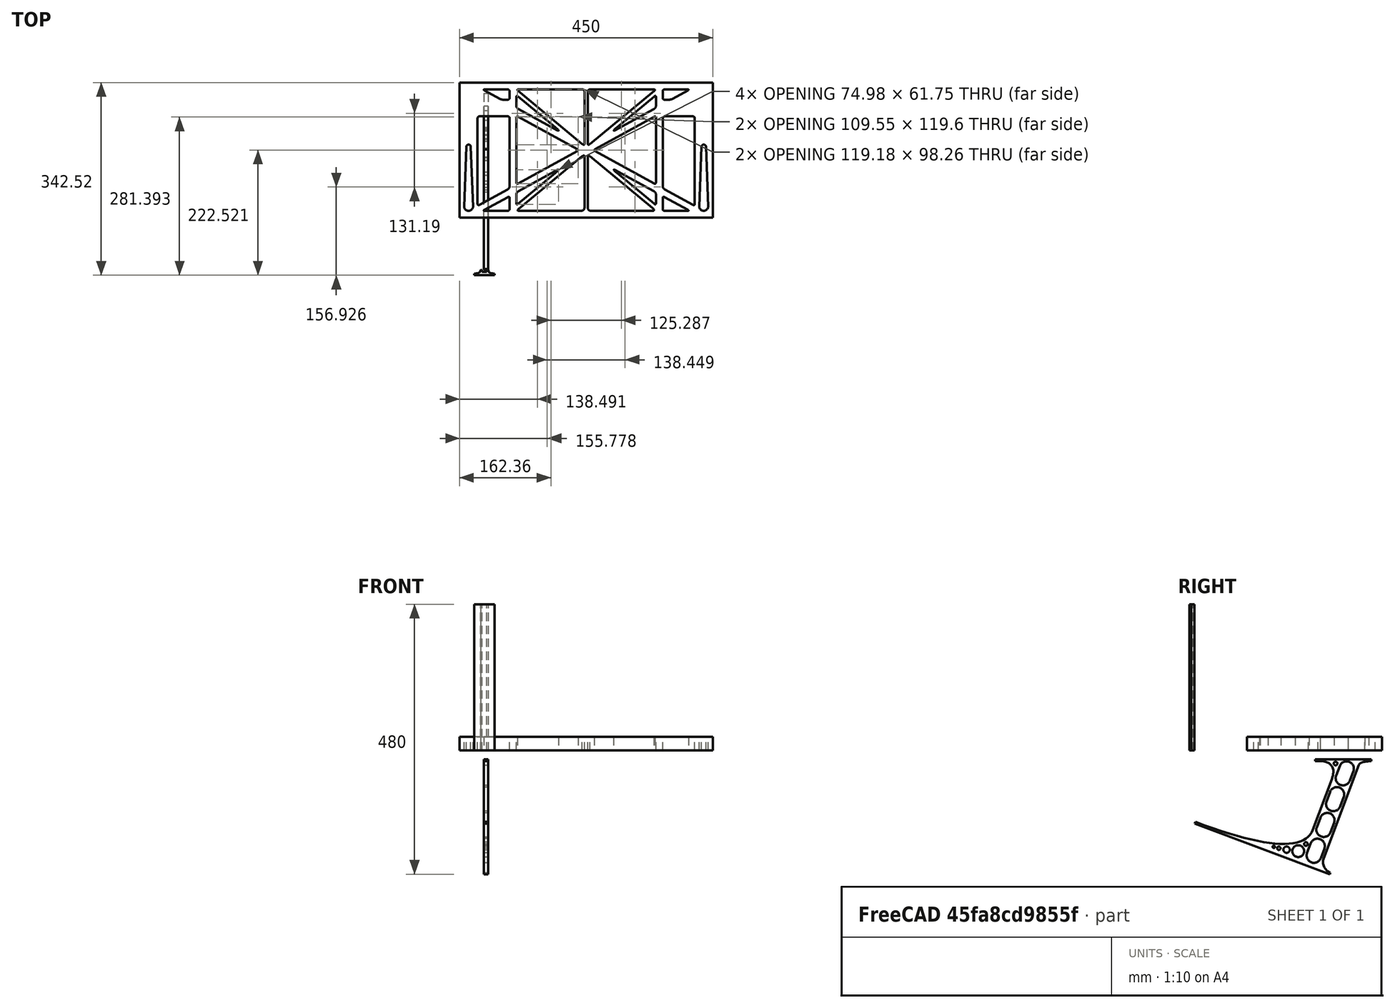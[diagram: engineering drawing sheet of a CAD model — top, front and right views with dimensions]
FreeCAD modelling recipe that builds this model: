
FCSTD DOCUMENT  (FreeCAD 0.19R0.19.2)
Label: laptopStand153FCStd
License: All rights reserved
LicenseURL: http://en.wikipedia.org/wiki/All_rights_reserved
objects: Sketcher::SketchObject×4, Part::Extrusion×3
note: 7 computed .brp shape members not serialized (recipe doc carries the construction recipe); baked Part::Feature solids carry a one-line shape summary decoded from their .brp

FEATURE [Sketcher::SketchObject] Sketch
  FullyConstrained = false
  sketch-geometry (349):
    g0: LineSegment StartX=-10.9272 StartY=-82.7794 StartZ=0 EndX=46.0728 EndY=-51.4823 EndZ=0
    g1: LineSegment StartX=-10.9272 StartY=76.4095 StartZ=0 EndX=-10.9272 EndY=-82.7794 EndZ=0
    g2: LineSegment StartX=46.0728 StartY=76.4095 StartZ=0 EndX=46.0728 EndY=-51.4823 EndZ=0
    g3: LineSegment StartX=-42.9272 StartY=136.221 StartZ=0 EndX=-42.9272 EndY=-103.779 EndZ=0
    g4: LineSegment StartX=407.073 StartY=136.221 StartZ=0 EndX=407.073 EndY=-103.779 EndZ=0
    g5: ArcOfCircle CenterX=-26.9272 CenterY=-83.7794 CenterZ=0 NormalX=0 NormalY=0 NormalZ=1 AngleXU=0 Radius=8 StartAngle=3.14159 EndAngle=6.28319
    g6: ArcOfCircle CenterX=391.073 CenterY=22.1087 CenterZ=0 NormalX=0 NormalY=0 NormalZ=1 AngleXU=0 Radius=8 StartAngle=-4.4e-15 EndAngle=3.14159
    g7: LineSegment StartX=399.073 StartY=22.1087 StartZ=0 EndX=399.073 EndY=-83.7794 EndZ=0
    g8: LineSegment StartX=383.073 StartY=22.1087 StartZ=0 EndX=383.073 EndY=-83.7794 EndZ=0
    g9: ArcOfCircle CenterX=391.073 CenterY=-83.7794 CenterZ=0 NormalX=0 NormalY=0 NormalZ=1 AngleXU=0 Radius=8 StartAngle=3.14159 EndAngle=6.28319
    g10: Circle CenterX=175.022 CenterY=27.0628 CenterZ=0 NormalX=0 NormalY=0 NormalZ=1 AngleXU=0 Radius=1
    g11: Circle CenterX=179.022 CenterY=24.8665 CenterZ=0 NormalX=0 NormalY=0 NormalZ=1 AngleXU=0 Radius=1
    g12: Circle CenterX=179.022 CenterY=27.0628 CenterZ=0 NormalX=0 NormalY=0 NormalZ=1 AngleXU=0 Radius=1
    g13: BSplineCurve PolesCount=3 KnotsCount=2 Degree=2 IsPeriodic=0
    g14: GeomPoint X=175.022 Y=27.0628 Z=0
    g15: GeomPoint X=179.022 Y=27.0628 Z=0
    g16: Circle CenterX=189.124 CenterY=27.0628 CenterZ=0 NormalX=0 NormalY=0 NormalZ=1 AngleXU=0 Radius=1
    g17: Circle CenterX=185.124 CenterY=24.8665 CenterZ=0 NormalX=0 NormalY=0 NormalZ=1 AngleXU=0 Radius=1
    g18: Circle CenterX=185.124 CenterY=27.0628 CenterZ=0 NormalX=0 NormalY=0 NormalZ=1 AngleXU=0 Radius=1
    g19: BSplineCurve PolesCount=3 KnotsCount=2 Degree=2 IsPeriodic=0
    g20: GeomPoint X=189.124 Y=27.0628 Z=0
    g21: GeomPoint X=185.124 Y=27.0628 Z=0
    g22: Circle CenterX=175.022 CenterY=5.37834 CenterZ=0 NormalX=0 NormalY=0 NormalZ=1 AngleXU=0 Radius=1
    g23: Circle CenterX=179.022 CenterY=7.57463 CenterZ=0 NormalX=0 NormalY=0 NormalZ=1 AngleXU=0 Radius=1
    g24: Circle CenterX=179.022 CenterY=5.34704 CenterZ=0 NormalX=0 NormalY=0 NormalZ=1 AngleXU=0 Radius=1
    g25: BSplineCurve PolesCount=3 KnotsCount=2 Degree=2 IsPeriodic=0
    g26: GeomPoint X=175.022 Y=5.37834 Z=0
    g27: GeomPoint X=179.022 Y=5.34704 Z=0
    g28: Circle CenterX=189.124 CenterY=5.37834 CenterZ=0 NormalX=0 NormalY=0 NormalZ=1 AngleXU=0 Radius=1
    g29: Circle CenterX=185.124 CenterY=7.57463 CenterZ=0 NormalX=0 NormalY=0 NormalZ=1 AngleXU=0 Radius=1
    g30: Circle CenterX=185.124 CenterY=5.34704 CenterZ=0 NormalX=0 NormalY=0 NormalZ=1 AngleXU=0 Radius=1
    g31: BSplineCurve PolesCount=3 KnotsCount=2 Degree=2 IsPeriodic=0
    g32: GeomPoint X=189.124 Y=5.37834 Z=0
    g33: GeomPoint X=185.124 Y=5.34704 Z=0
    g34: Circle CenterX=165.871 CenterY=18.1458 CenterZ=0 NormalX=0 NormalY=0 NormalZ=1 AngleXU=0 Radius=1
    g35: Circle CenterX=169.377 CenterY=16.2206 CenterZ=0 NormalX=0 NormalY=0 NormalZ=1 AngleXU=0 Radius=1
    g36: Circle CenterX=165.871 CenterY=14.2954 CenterZ=0 NormalX=0 NormalY=0 NormalZ=1 AngleXU=0 Radius=1
    g37: BSplineCurve PolesCount=3 KnotsCount=2 Degree=2 IsPeriodic=0
    g38: GeomPoint X=165.871 Y=18.1458 Z=0
    g39: GeomPoint X=165.871 Y=14.2954 Z=0
    g40: Circle CenterX=198.275 CenterY=18.1458 CenterZ=0 NormalX=0 NormalY=0 NormalZ=1 AngleXU=0 Radius=1
    g41: Circle CenterX=194.768 CenterY=16.2206 CenterZ=0 NormalX=0 NormalY=0 NormalZ=1 AngleXU=0 Radius=1
    g42: Circle CenterX=198.275 CenterY=14.2954 CenterZ=0 NormalX=0 NormalY=0 NormalZ=1 AngleXU=0 Radius=1
    g43: BSplineCurve PolesCount=3 KnotsCount=2 Degree=2 IsPeriodic=0
    g44: GeomPoint X=198.275 Y=18.1458 Z=0
    g45: GeomPoint X=198.275 Y=14.2954 Z=0
    g46: LineSegment StartX=407.073 StartY=-103.779 StartZ=0 EndX=-42.9272 EndY=-103.779 EndZ=0
    g47: LineSegment StartX=407.073 StartY=136.221 StartZ=0 EndX=-42.9272 EndY=136.221 EndZ=0
    g48: LineSegment StartX=46.0728 StartY=76.4095 StartZ=0 EndX=-10.9272 EndY=76.4095 EndZ=0
    g49: Circle CenterX=125.607 CenterY=54.1951 CenterZ=0 NormalX=0 NormalY=0 NormalZ=1 AngleXU=0 Radius=1
    g50: Circle CenterX=139.632 CenterY=46.4944 CenterZ=0 NormalX=0 NormalY=0 NormalZ=1 AngleXU=0 Radius=1
    g51: Circle CenterX=127.326 CenterY=56.7187 CenterZ=0 NormalX=0 NormalY=0 NormalZ=1 AngleXU=0 Radius=1
    g52: BSplineCurve PolesCount=3 KnotsCount=2 Degree=2 IsPeriodic=0
    g53: GeomPoint X=125.607 Y=54.1951 Z=0
    g54: GeomPoint X=127.326 Y=56.7187 Z=0
    g55: Circle CenterX=236.821 CenterY=56.7187 CenterZ=0 NormalX=0 NormalY=0 NormalZ=1 AngleXU=0 Radius=1
    g56: Circle CenterX=224.513 CenterY=46.4944 CenterZ=0 NormalX=0 NormalY=0 NormalZ=1 AngleXU=0 Radius=1
    g57: Circle CenterX=238.538 CenterY=54.1951 CenterZ=0 NormalX=0 NormalY=0 NormalZ=1 AngleXU=0 Radius=1
    g58: BSplineCurve PolesCount=3 KnotsCount=2 Degree=2 IsPeriodic=0
    g59: GeomPoint X=236.821 Y=56.7187 Z=0
    g60: GeomPoint X=238.538 Y=54.1951 Z=0
    g61: Circle CenterX=238.538 CenterY=-21.7539 CenterZ=0 NormalX=0 NormalY=0 NormalZ=1 AngleXU=0 Radius=1
    g62: Circle CenterX=224.513 CenterY=-14.0532 CenterZ=0 NormalX=0 NormalY=0 NormalZ=1 AngleXU=0 Radius=1
    g63: Circle CenterX=236.821 CenterY=-24.2775 CenterZ=0 NormalX=0 NormalY=0 NormalZ=1 AngleXU=0 Radius=1
    g64: BSplineCurve PolesCount=3 KnotsCount=2 Degree=2 IsPeriodic=0
    g65: GeomPoint X=238.538 Y=-21.7539 Z=0
    g66: GeomPoint X=236.821 Y=-24.2775 Z=0
    g67: Circle CenterX=125.607 CenterY=-21.7539 CenterZ=0 NormalX=0 NormalY=0 NormalZ=1 AngleXU=0 Radius=1
    g68: Circle CenterX=139.632 CenterY=-14.0532 CenterZ=0 NormalX=0 NormalY=0 NormalZ=1 AngleXU=0 Radius=1
    g69: Circle CenterX=127.325 CenterY=-24.2775 CenterZ=0 NormalX=0 NormalY=0 NormalZ=1 AngleXU=0 Radius=1
    g70: BSplineCurve PolesCount=3 KnotsCount=2 Degree=2 IsPeriodic=0
    g71: GeomPoint X=125.607 Y=-21.7539 Z=0
    g72: GeomPoint X=127.325 Y=-24.2775 Z=0
    g73: Circle CenterX=302.996 CenterY=111.695 CenterZ=0 NormalX=0 NormalY=0 NormalZ=1 AngleXU=0 Radius=1
    g74: Circle CenterX=306.073 CenterY=114.251 CenterZ=0 NormalX=0 NormalY=0 NormalZ=1 AngleXU=0 Radius=1
    g75: Circle CenterX=306.073 CenterY=110.251 CenterZ=0 NormalX=0 NormalY=0 NormalZ=1 AngleXU=0 Radius=1
    g76: BSplineCurve PolesCount=3 KnotsCount=2 Degree=2 IsPeriodic=0
    g77: GeomPoint X=302.996 Y=111.695 Z=0
    g78: GeomPoint X=306.073 Y=110.251 Z=0
    g79: Circle CenterX=306.073 CenterY=95.2763 CenterZ=0 NormalX=0 NormalY=0 NormalZ=1 AngleXU=0 Radius=1
    g80: Circle CenterX=306.073 CenterY=91.2763 CenterZ=0 NormalX=0 NormalY=0 NormalZ=1 AngleXU=0 Radius=1
    g81: Circle CenterX=302.567 CenterY=89.3511 CenterZ=0 NormalX=0 NormalY=0 NormalZ=1 AngleXU=0 Radius=1
    g82: BSplineCurve PolesCount=3 KnotsCount=2 Degree=2 IsPeriodic=0
    g83: GeomPoint X=306.073 Y=95.2763 Z=0
    g84: GeomPoint X=302.567 Y=89.3511 Z=0
    g85: LineSegment StartX=306.073 StartY=110.251 StartZ=0 EndX=306.073 EndY=95.2763 EndZ=0
    g86: LineSegment StartX=302.996 StartY=111.695 StartZ=0 EndX=236.821 EndY=56.7187 EndZ=0
    g87: LineSegment StartX=238.538 StartY=54.1951 StartZ=0 EndX=302.567 EndY=89.3511 EndZ=0
    g88: Circle CenterX=61.1496 CenterY=111.695 CenterZ=0 NormalX=0 NormalY=0 NormalZ=1 AngleXU=0 Radius=1
    g89: Circle CenterX=58.0728 CenterY=114.251 CenterZ=0 NormalX=0 NormalY=0 NormalZ=1 AngleXU=0 Radius=1
    g90: Circle CenterX=58.0728 CenterY=110.251 CenterZ=0 NormalX=0 NormalY=0 NormalZ=1 AngleXU=0 Radius=1
    g91: BSplineCurve PolesCount=3 KnotsCount=2 Degree=2 IsPeriodic=0
    g92: GeomPoint X=61.1496 Y=111.695 Z=0
    g93: GeomPoint X=58.0728 Y=110.251 Z=0
    g94: Circle CenterX=61.5791 CenterY=89.3511 CenterZ=0 NormalX=0 NormalY=0 NormalZ=1 AngleXU=0 Radius=1
    g95: Circle CenterX=58.0728 CenterY=91.2763 CenterZ=0 NormalX=0 NormalY=0 NormalZ=1 AngleXU=0 Radius=1
    g96: Circle CenterX=58.0728 CenterY=95.2763 CenterZ=0 NormalX=0 NormalY=0 NormalZ=1 AngleXU=0 Radius=1
    g97: BSplineCurve PolesCount=3 KnotsCount=2 Degree=2 IsPeriodic=0
    g98: GeomPoint X=61.5791 Y=89.3511 Z=0
    g99: GeomPoint X=58.0728 Y=95.2763 Z=0
    g100: LineSegment StartX=58.0728 StartY=110.251 StartZ=0 EndX=58.0728 EndY=95.2763 EndZ=0
    g101: LineSegment StartX=61.1496 StartY=111.695 StartZ=0 EndX=127.326 EndY=56.7187 EndZ=0
    g102: LineSegment StartX=125.607 StartY=54.1951 StartZ=0 EndX=61.5791 EndY=89.3511 EndZ=0
    g103: Circle CenterX=61.5791 CenterY=-56.9099 CenterZ=0 NormalX=0 NormalY=0 NormalZ=1 AngleXU=0 Radius=1
    g104: Circle CenterX=58.0728 CenterY=-58.8351 CenterZ=0 NormalX=0 NormalY=0 NormalZ=1 AngleXU=0 Radius=1
    g105: Circle CenterX=58.0728 CenterY=-62.8351 CenterZ=0 NormalX=0 NormalY=0 NormalZ=1 AngleXU=0 Radius=1
    g106: BSplineCurve PolesCount=3 KnotsCount=2 Degree=2 IsPeriodic=0
    g107: GeomPoint X=61.5791 Y=-56.9099 Z=0
    g108: GeomPoint X=58.0728 Y=-62.8351 Z=0
    g109: Circle CenterX=58.0728 CenterY=-77.8102 CenterZ=0 NormalX=0 NormalY=0 NormalZ=1 AngleXU=0 Radius=1
    g110: Circle CenterX=58.0728 CenterY=-81.8102 CenterZ=0 NormalX=0 NormalY=0 NormalZ=1 AngleXU=0 Radius=1
    g111: Circle CenterX=61.1496 CenterY=-79.2541 CenterZ=0 NormalX=0 NormalY=0 NormalZ=1 AngleXU=0 Radius=1
    g112: BSplineCurve PolesCount=3 KnotsCount=2 Degree=2 IsPeriodic=0
    g113: GeomPoint X=58.0728 Y=-77.8102 Z=0
    g114: GeomPoint X=61.1496 Y=-79.2541 Z=0
    g115: LineSegment StartX=58.0728 StartY=-62.8351 StartZ=0 EndX=58.0728 EndY=-77.8102 EndZ=0
    g116: LineSegment StartX=61.1496 StartY=-79.2541 StartZ=0 EndX=127.325 EndY=-24.2775 EndZ=0
    g117: LineSegment StartX=125.607 StartY=-21.7539 StartZ=0 EndX=61.5791 EndY=-56.9099 EndZ=0
    g118: Circle CenterX=302.567 CenterY=-56.9099 CenterZ=0 NormalX=0 NormalY=0 NormalZ=1 AngleXU=0 Radius=1
    g119: Circle CenterX=306.073 CenterY=-58.8351 CenterZ=0 NormalX=0 NormalY=0 NormalZ=1 AngleXU=0 Radius=1
    g120: Circle CenterX=306.073 CenterY=-62.8351 CenterZ=0 NormalX=0 NormalY=0 NormalZ=1 AngleXU=0 Radius=1
    g121: BSplineCurve PolesCount=3 KnotsCount=2 Degree=2 IsPeriodic=0
    g122: GeomPoint X=302.567 Y=-56.9099 Z=0
    g123: GeomPoint X=306.073 Y=-62.8351 Z=0
    g124: Circle CenterX=302.996 CenterY=-79.2541 CenterZ=0 NormalX=0 NormalY=0 NormalZ=1 AngleXU=0 Radius=1
    g125: Circle CenterX=306.073 CenterY=-81.8102 CenterZ=0 NormalX=0 NormalY=0 NormalZ=1 AngleXU=0 Radius=1
    g126: Circle CenterX=306.073 CenterY=-77.8102 CenterZ=0 NormalX=0 NormalY=0 NormalZ=1 AngleXU=0 Radius=1
    g127: BSplineCurve PolesCount=3 KnotsCount=2 Degree=2 IsPeriodic=0
    g128: GeomPoint X=302.996 Y=-79.2541 Z=0
    g129: GeomPoint X=306.073 Y=-77.8102 Z=0
    g130: LineSegment StartX=306.073 StartY=-62.8351 StartZ=0 EndX=306.073 EndY=-77.8102 EndZ=0
    g131: LineSegment StartX=302.996 StartY=-79.2541 StartZ=0 EndX=236.821 EndY=-24.2775 EndZ=0
    g132: LineSegment StartX=238.538 StartY=-21.7539 StartZ=0 EndX=302.567 EndY=-56.9099 EndZ=0
    g133: Circle CenterX=61.6457 CenterY=-88.8112 CenterZ=0 NormalX=0 NormalY=0 NormalZ=1 AngleXU=0 Radius=1
    g134: Circle CenterX=58.0728 CenterY=-91.7794 CenterZ=0 NormalX=0 NormalY=0 NormalZ=1 AngleXU=0 Radius=1
    g135: Circle CenterX=63.9135 CenterY=-91.7794 CenterZ=0 NormalX=0 NormalY=0 NormalZ=1 AngleXU=0 Radius=1
    g136: BSplineCurve PolesCount=3 KnotsCount=2 Degree=2 IsPeriodic=0
    g137: GeomPoint X=61.6457 Y=-88.8112 Z=0
    g138: GeomPoint X=63.9135 Y=-91.7794 Z=0
    g139: Circle CenterX=179.022 CenterY=-85.8163 CenterZ=0 NormalX=0 NormalY=0 NormalZ=1 AngleXU=0 Radius=1
    g140: Circle CenterX=179.022 CenterY=-91.7794 CenterZ=0 NormalX=0 NormalY=0 NormalZ=1 AngleXU=0 Radius=1
    g141: Circle CenterX=171.895 CenterY=-91.7794 CenterZ=0 NormalX=0 NormalY=0 NormalZ=1 AngleXU=0 Radius=1
    g142: BSplineCurve PolesCount=3 KnotsCount=2 Degree=2 IsPeriodic=0
    g143: GeomPoint X=179.022 Y=-85.8163 Z=0
    g144: GeomPoint X=171.895 Y=-91.7794 Z=0
    g145: Circle CenterX=185.124 CenterY=-86.2028 CenterZ=0 NormalX=0 NormalY=0 NormalZ=1 AngleXU=0 Radius=1
    g146: Circle CenterX=185.124 CenterY=-91.7794 CenterZ=0 NormalX=0 NormalY=0 NormalZ=1 AngleXU=0 Radius=1
    g147: Circle CenterX=191.747 CenterY=-91.7794 CenterZ=0 NormalX=0 NormalY=0 NormalZ=1 AngleXU=0 Radius=1
    g148: BSplineCurve PolesCount=3 KnotsCount=2 Degree=2 IsPeriodic=0
    g149: GeomPoint X=185.124 Y=-86.2028 Z=0
    g150: GeomPoint X=191.747 Y=-91.7794 Z=0
    g151: Circle CenterX=299.888 CenterY=-86.6413 CenterZ=0 NormalX=0 NormalY=0 NormalZ=1 AngleXU=0 Radius=1
    g152: Circle CenterX=306.073 CenterY=-91.7794 CenterZ=0 NormalX=0 NormalY=0 NormalZ=1 AngleXU=0 Radius=1
    g153: Circle CenterX=298.776 CenterY=-91.7794 CenterZ=0 NormalX=0 NormalY=0 NormalZ=1 AngleXU=0 Radius=1
    g154: BSplineCurve PolesCount=3 KnotsCount=2 Degree=2 IsPeriodic=0
    g155: GeomPoint X=299.888 Y=-86.6413 Z=0
    g156: GeomPoint X=298.776 Y=-91.7794 Z=0
    g157: LineSegment StartX=189.124 StartY=5.37834 StartZ=0 EndX=299.888 EndY=-86.6413 EndZ=0
    g158: LineSegment StartX=298.776 StartY=-91.7794 StartZ=0 EndX=191.747 EndY=-91.7794 EndZ=0
    g159: LineSegment StartX=185.124 StartY=-86.2028 StartZ=0 EndX=185.124 EndY=5.34704 EndZ=0
    g160: LineSegment StartX=179.022 StartY=5.34704 StartZ=0 EndX=179.022 EndY=-85.8163 EndZ=0
    g161: LineSegment StartX=171.895 StartY=-91.7794 StartZ=0 EndX=63.9135 EndY=-91.7794 EndZ=0
    g162: LineSegment StartX=61.6457 StartY=-88.8112 StartZ=0 EndX=175.022 EndY=5.37834 EndZ=0
    g163: Circle CenterX=302.073 CenterY=124.221 CenterZ=0 NormalX=0 NormalY=0 NormalZ=1 AngleXU=0 Radius=1
    g164: Circle CenterX=306.073 CenterY=124.221 CenterZ=0 NormalX=0 NormalY=0 NormalZ=1 AngleXU=0 Radius=1
    g165: Circle CenterX=302.996 CenterY=121.665 CenterZ=0 NormalX=0 NormalY=0 NormalZ=1 AngleXU=0 Radius=1
    g166: BSplineCurve PolesCount=3 KnotsCount=2 Degree=2 IsPeriodic=0
    g167: GeomPoint X=302.073 Y=124.221 Z=0
    g168: GeomPoint X=302.996 Y=121.665 Z=0
    g169: Circle CenterX=189.124 CenterY=124.221 CenterZ=0 NormalX=0 NormalY=0 NormalZ=1 AngleXU=0 Radius=1
    g170: Circle CenterX=185.124 CenterY=124.221 CenterZ=0 NormalX=0 NormalY=0 NormalZ=1 AngleXU=0 Radius=1
    g171: Circle CenterX=185.124 CenterY=120.221 CenterZ=0 NormalX=0 NormalY=0 NormalZ=1 AngleXU=0 Radius=1
    g172: BSplineCurve PolesCount=3 KnotsCount=2 Degree=2 IsPeriodic=0
    g173: GeomPoint X=189.124 Y=124.221 Z=0
    g174: GeomPoint X=185.124 Y=120.221 Z=0
    g175: Circle CenterX=175.022 CenterY=124.221 CenterZ=0 NormalX=0 NormalY=0 NormalZ=1 AngleXU=0 Radius=1
    g176: Circle CenterX=179.022 CenterY=124.221 CenterZ=0 NormalX=0 NormalY=0 NormalZ=1 AngleXU=0 Radius=1
    g177: Circle CenterX=179.022 CenterY=120.221 CenterZ=0 NormalX=0 NormalY=0 NormalZ=1 AngleXU=0 Radius=1
    g178: BSplineCurve PolesCount=3 KnotsCount=2 Degree=2 IsPeriodic=0
    g179: GeomPoint X=175.022 Y=124.221 Z=0
    g180: GeomPoint X=179.022 Y=120.221 Z=0
    g181: Circle CenterX=62.0728 CenterY=124.221 CenterZ=0 NormalX=0 NormalY=0 NormalZ=1 AngleXU=0 Radius=1
    g182: Circle CenterX=58.0728 CenterY=124.221 CenterZ=0 NormalX=0 NormalY=0 NormalZ=1 AngleXU=0 Radius=1
    g183: Circle CenterX=61.1496 CenterY=121.665 CenterZ=0 NormalX=0 NormalY=0 NormalZ=1 AngleXU=0 Radius=1
    g184: BSplineCurve PolesCount=3 KnotsCount=2 Degree=2 IsPeriodic=0
    g185: GeomPoint X=62.0728 Y=124.221 Z=0
    g186: GeomPoint X=61.1496 Y=121.665 Z=0
    g187: LineSegment StartX=62.0728 StartY=124.221 StartZ=0 EndX=175.022 EndY=124.221 EndZ=0
    g188: LineSegment StartX=179.022 StartY=120.221 StartZ=0 EndX=179.022 EndY=27.0628 EndZ=0
    g189: LineSegment StartX=185.124 StartY=27.0628 StartZ=0 EndX=185.124 EndY=120.221 EndZ=0
    g190: LineSegment StartX=189.124 StartY=124.221 StartZ=0 EndX=302.073 EndY=124.221 EndZ=0
    g191: LineSegment StartX=302.996 StartY=121.665 StartZ=0 EndX=189.124 EndY=27.0628 EndZ=0
    g192: LineSegment StartX=175.022 StartY=27.0628 StartZ=0 EndX=61.1496 EndY=121.665 EndZ=0
    g193: Circle CenterX=61.5791 CenterY=75.4095 CenterZ=0 NormalX=0 NormalY=0 NormalZ=1 AngleXU=0 Radius=1
    g194: Circle CenterX=58.0728 CenterY=77.3346 CenterZ=0 NormalX=0 NormalY=0 NormalZ=1 AngleXU=0 Radius=1
    g195: Circle CenterX=58.0728 CenterY=73.3346 CenterZ=0 NormalX=0 NormalY=0 NormalZ=1 AngleXU=0 Radius=1
    g196: BSplineCurve PolesCount=3 KnotsCount=2 Degree=2 IsPeriodic=0
    g197: GeomPoint X=61.5791 Y=75.4095 Z=0
    g198: GeomPoint X=58.0728 Y=73.3346 Z=0
    g199: Circle CenterX=58.0728 CenterY=-40.8935 CenterZ=0 NormalX=0 NormalY=0 NormalZ=1 AngleXU=0 Radius=1
    g200: Circle CenterX=58.0728 CenterY=-44.8935 CenterZ=0 NormalX=0 NormalY=0 NormalZ=1 AngleXU=0 Radius=1
    g201: Circle CenterX=61.5791 CenterY=-42.9683 CenterZ=0 NormalX=0 NormalY=0 NormalZ=1 AngleXU=0 Radius=1
    g202: BSplineCurve PolesCount=3 KnotsCount=2 Degree=2 IsPeriodic=0
    g203: GeomPoint X=58.0728 Y=-40.8935 Z=0
    g204: GeomPoint X=61.5791 Y=-42.9683 Z=0
    g205: LineSegment StartX=61.5791 StartY=-42.9683 StartZ=0 EndX=165.871 EndY=14.2954 EndZ=0
    g206: LineSegment StartX=165.871 StartY=18.1458 StartZ=0 EndX=61.5791 EndY=75.4095 EndZ=0
    g207: LineSegment StartX=58.0728 StartY=73.3346 StartZ=0 EndX=58.0728 EndY=-40.8935 EndZ=0
    g208: Circle CenterX=302.567 CenterY=-42.9683 CenterZ=0 NormalX=0 NormalY=0 NormalZ=1 AngleXU=0 Radius=1
    g209: Circle CenterX=306.073 CenterY=-44.8935 CenterZ=0 NormalX=0 NormalY=0 NormalZ=1 AngleXU=0 Radius=1
    g210: Circle CenterX=306.073 CenterY=-40.8935 CenterZ=0 NormalX=0 NormalY=0 NormalZ=1 AngleXU=0 Radius=1
    g211: BSplineCurve PolesCount=3 KnotsCount=2 Degree=2 IsPeriodic=0
    g212: GeomPoint X=302.567 Y=-42.9683 Z=0
    g213: GeomPoint X=306.073 Y=-40.8935 Z=0
    g214: Circle CenterX=306.073 CenterY=73.3346 CenterZ=0 NormalX=0 NormalY=0 NormalZ=1 AngleXU=0 Radius=1
    g215: Circle CenterX=306.073 CenterY=77.3346 CenterZ=0 NormalX=0 NormalY=0 NormalZ=1 AngleXU=0 Radius=1
    g216: Circle CenterX=302.567 CenterY=75.4095 CenterZ=0 NormalX=0 NormalY=0 NormalZ=1 AngleXU=0 Radius=1
    g217: BSplineCurve PolesCount=3 KnotsCount=2 Degree=2 IsPeriodic=0
    g218: GeomPoint X=306.073 Y=73.3346 Z=0
    g219: GeomPoint X=302.567 Y=75.4095 Z=0
    g220: LineSegment StartX=302.567 StartY=-42.9683 StartZ=0 EndX=198.275 EndY=14.2954 EndZ=0
    g221: LineSegment StartX=198.275 StartY=18.1458 StartZ=0 EndX=302.567 EndY=75.4095 EndZ=0
    g222: LineSegment StartX=306.073 StartY=73.3346 StartZ=0 EndX=306.073 EndY=-40.8935 EndZ=0
    g223: LineSegment StartX=322.073 StartY=105.865 StartZ=0 EndX=328.643 EndY=105.865 EndZ=0
    g224: LineSegment StartX=318.073 StartY=120.221 StartZ=0 EndX=318.073 EndY=109.865 EndZ=0
    g225: LineSegment StartX=336.157 StartY=107.779 StartZ=0 EndX=362.567 EndY=122.294 EndZ=0
    g226: Circle CenterX=362.073 CenterY=124.221 CenterZ=0 NormalX=0 NormalY=0 NormalZ=1 AngleXU=0 Radius=1
    g227: Circle CenterX=366.073 CenterY=124.221 CenterZ=0 NormalX=0 NormalY=0 NormalZ=1 AngleXU=0 Radius=1
    g228: Circle CenterX=362.567 CenterY=122.294 CenterZ=0 NormalX=0 NormalY=0 NormalZ=1 AngleXU=0 Radius=1
    g229: BSplineCurve PolesCount=3 KnotsCount=2 Degree=2 IsPeriodic=0
    g230: GeomPoint X=362.073 Y=124.221 Z=0
    g231: GeomPoint X=362.567 Y=122.294 Z=0
    g232: Circle CenterX=322.073 CenterY=124.221 CenterZ=0 NormalX=0 NormalY=0 NormalZ=1 AngleXU=0 Radius=1
    g233: Circle CenterX=318.073 CenterY=124.221 CenterZ=0 NormalX=0 NormalY=0 NormalZ=1 AngleXU=0 Radius=1
    g234: Circle CenterX=318.073 CenterY=120.221 CenterZ=0 NormalX=0 NormalY=0 NormalZ=1 AngleXU=0 Radius=1
    g235: BSplineCurve PolesCount=3 KnotsCount=2 Degree=2 IsPeriodic=0
    g236: GeomPoint X=322.073 Y=124.221 Z=0
    g237: GeomPoint X=318.073 Y=120.221 Z=0
    g238: Circle CenterX=322.073 CenterY=105.865 CenterZ=0 NormalX=0 NormalY=0 NormalZ=1 AngleXU=0 Radius=1
    g239: Circle CenterX=318.073 CenterY=105.865 CenterZ=0 NormalX=0 NormalY=0 NormalZ=1 AngleXU=0 Radius=1
    g240: Circle CenterX=318.073 CenterY=109.865 CenterZ=0 NormalX=0 NormalY=0 NormalZ=1 AngleXU=0 Radius=1
    g241: BSplineCurve PolesCount=3 KnotsCount=2 Degree=2 IsPeriodic=0
    g242: GeomPoint X=322.073 Y=105.865 Z=0
    g243: GeomPoint X=318.073 Y=109.865 Z=0
    g244: Circle CenterX=336.157 CenterY=107.779 CenterZ=0 NormalX=0 NormalY=0 NormalZ=1 AngleXU=0 Radius=1
    g245: Circle CenterX=332.651 CenterY=105.853 CenterZ=0 NormalX=0 NormalY=0 NormalZ=1 AngleXU=0 Radius=1
    g246: Circle CenterX=328.643 CenterY=105.865 CenterZ=0 NormalX=0 NormalY=0 NormalZ=1 AngleXU=0 Radius=1
    g247: BSplineCurve PolesCount=3 KnotsCount=2 Degree=2 IsPeriodic=0
    g248: GeomPoint X=336.157 Y=107.779 Z=0
    g249: GeomPoint X=328.643 Y=105.865 Z=0
    g250: LineSegment StartX=322.073 StartY=124.221 StartZ=0 EndX=362.073 EndY=124.221 EndZ=0
    g251: Circle CenterX=371.567 CenterY=-80.8644 CenterZ=0 NormalX=0 NormalY=0 NormalZ=1 AngleXU=0 Radius=1
    g252: Circle CenterX=375.073 CenterY=-82.7896 CenterZ=0 NormalX=0 NormalY=0 NormalZ=1 AngleXU=0 Radius=1
    g253: Circle CenterX=375.073 CenterY=-78.7896 CenterZ=0 NormalX=0 NormalY=0 NormalZ=1 AngleXU=0 Radius=1
    g254: BSplineCurve PolesCount=3 KnotsCount=2 Degree=2 IsPeriodic=0
    g255: GeomPoint X=371.567 Y=-80.8644 Z=0
    g256: GeomPoint X=375.073 Y=-78.7896 Z=0
    g257: Circle CenterX=321.579 CenterY=-53.4075 CenterZ=0 NormalX=0 NormalY=0 NormalZ=1 AngleXU=0 Radius=1
    g258: Circle CenterX=318.073 CenterY=-51.4823 CenterZ=0 NormalX=0 NormalY=0 NormalZ=1 AngleXU=0 Radius=1
    g259: Circle CenterX=318.073 CenterY=-47.4805 CenterZ=0 NormalX=0 NormalY=0 NormalZ=1 AngleXU=0 Radius=1
    g260: BSplineCurve PolesCount=3 KnotsCount=2 Degree=2 IsPeriodic=0
    g261: GeomPoint X=321.579 Y=-53.4075 Z=0
    g262: GeomPoint X=318.073 Y=-47.4805 Z=0
    g263: LineSegment StartX=371.567 StartY=-80.8644 StartZ=0 EndX=321.579 EndY=-53.4075 EndZ=0
    g264: Circle CenterX=321.579 CenterY=-67.3492 CenterZ=0 NormalX=0 NormalY=0 NormalZ=1 AngleXU=0 Radius=1
    g265: Circle CenterX=318.073 CenterY=-65.424 CenterZ=0 NormalX=0 NormalY=0 NormalZ=1 AngleXU=0 Radius=1
    g266: Circle CenterX=318.073 CenterY=-69.424 CenterZ=0 NormalX=0 NormalY=0 NormalZ=1 AngleXU=0 Radius=1
    g267: BSplineCurve PolesCount=3 KnotsCount=2 Degree=2 IsPeriodic=0
    g268: GeomPoint X=321.579 Y=-67.3492 Z=0
    g269: GeomPoint X=318.073 Y=-69.424 Z=0
    g270: Circle CenterX=362.567 CenterY=-89.8542 CenterZ=0 NormalX=0 NormalY=0 NormalZ=1 AngleXU=0 Radius=1
    g271: Circle CenterX=366.073 CenterY=-91.7794 CenterZ=0 NormalX=0 NormalY=0 NormalZ=1 AngleXU=0 Radius=1
    g272: Circle CenterX=362.073 CenterY=-91.7794 CenterZ=0 NormalX=0 NormalY=0 NormalZ=1 AngleXU=0 Radius=1
    g273: BSplineCurve PolesCount=3 KnotsCount=2 Degree=2 IsPeriodic=0
    g274: GeomPoint X=362.567 Y=-89.8542 Z=0
    g275: GeomPoint X=362.073 Y=-91.7794 Z=0
    g276: Circle CenterX=322.073 CenterY=-91.7794 CenterZ=0 NormalX=0 NormalY=0 NormalZ=1 AngleXU=0 Radius=1
    g277: Circle CenterX=318.073 CenterY=-91.7794 CenterZ=0 NormalX=0 NormalY=0 NormalZ=1 AngleXU=0 Radius=1
    g278: Circle CenterX=318.073 CenterY=-87.7794 CenterZ=0 NormalX=0 NormalY=0 NormalZ=1 AngleXU=0 Radius=1
    g279: BSplineCurve PolesCount=3 KnotsCount=2 Degree=2 IsPeriodic=0
    g280: GeomPoint X=322.073 Y=-91.7794 Z=0
    g281: GeomPoint X=318.073 Y=-87.7794 Z=0
    g282: LineSegment StartX=362.567 StartY=-89.8542 StartZ=0 EndX=321.579 EndY=-67.3492 EndZ=0
    g283: LineSegment StartX=318.073 StartY=-69.424 StartZ=0 EndX=318.073 EndY=-87.7794 EndZ=0
    g284: LineSegment StartX=322.073 StartY=-91.7794 StartZ=0 EndX=362.073 EndY=-91.7794 EndZ=0
    g285: Circle CenterX=2.07281 CenterY=124.221 CenterZ=0 NormalX=0 NormalY=0 NormalZ=1 AngleXU=0 Radius=1
    g286: Circle CenterX=1.57905 CenterY=122.295 CenterZ=0 NormalX=0 NormalY=0 NormalZ=1 AngleXU=0 Radius=1
    g287: BSplineCurve PolesCount=3 KnotsCount=2 Degree=2 IsPeriodic=0
    g288: GeomPoint X=2.07281 Y=124.221 Z=0
    g289: GeomPoint X=1.57905 Y=122.295 Z=0
    g290: Circle CenterX=42.0728 CenterY=124.221 CenterZ=0 NormalX=0 NormalY=0 NormalZ=1 AngleXU=0 Radius=1
    g291: Circle CenterX=46.0728 CenterY=124.221 CenterZ=0 NormalX=0 NormalY=0 NormalZ=1 AngleXU=0 Radius=1
    g292: Circle CenterX=46.0728 CenterY=120.221 CenterZ=0 NormalX=0 NormalY=0 NormalZ=1 AngleXU=0 Radius=1
    g293: BSplineCurve PolesCount=3 KnotsCount=2 Degree=2 IsPeriodic=0
    g294: GeomPoint X=42.0728 Y=124.221 Z=0
    g295: GeomPoint X=46.0728 Y=120.221 Z=0
    g296: Circle CenterX=46.0728 CenterY=109.865 CenterZ=0 NormalX=0 NormalY=0 NormalZ=1 AngleXU=0 Radius=1
    g297: Circle CenterX=46.0728 CenterY=105.865 CenterZ=0 NormalX=0 NormalY=0 NormalZ=1 AngleXU=0 Radius=1
    g298: Circle CenterX=42.0728 CenterY=105.865 CenterZ=0 NormalX=0 NormalY=0 NormalZ=1 AngleXU=0 Radius=1
    g299: BSplineCurve PolesCount=3 KnotsCount=2 Degree=2 IsPeriodic=0
    g300: GeomPoint X=46.0728 Y=109.865 Z=0
    g301: GeomPoint X=42.0728 Y=105.865 Z=0
    g302: Circle CenterX=35.5028 CenterY=105.865 CenterZ=0 NormalX=0 NormalY=0 NormalZ=1 AngleXU=0 Radius=1
    g303: Circle CenterX=31.5028 CenterY=105.865 CenterZ=0 NormalX=0 NormalY=0 NormalZ=1 AngleXU=0 Radius=1
    g304: Circle CenterX=27.9965 CenterY=107.79 CenterZ=0 NormalX=0 NormalY=0 NormalZ=1 AngleXU=0 Radius=1
    g305: BSplineCurve PolesCount=3 KnotsCount=2 Degree=2 IsPeriodic=0
    g306: GeomPoint X=35.5028 Y=105.865 Z=0
    g307: GeomPoint X=27.9965 Y=107.79 Z=0
    g308: LineSegment StartX=2.07281 StartY=124.221 StartZ=0 EndX=42.0728 EndY=124.221 EndZ=0
    g309: LineSegment StartX=46.0728 StartY=120.221 StartZ=0 EndX=46.0728 EndY=109.865 EndZ=0
    g310: LineSegment StartX=42.0728 StartY=105.865 StartZ=0 EndX=35.5028 EndY=105.865 EndZ=0
    g311: LineSegment StartX=27.9965 StartY=107.79 StartZ=0 EndX=1.57905 EndY=122.295 EndZ=0
    g312: Circle CenterX=42.5666 CenterY=-67.3492 CenterZ=0 NormalX=0 NormalY=0 NormalZ=1 AngleXU=0 Radius=1
    g313: Circle CenterX=46.0728 CenterY=-65.424 CenterZ=0 NormalX=0 NormalY=0 NormalZ=1 AngleXU=0 Radius=1
    g314: Circle CenterX=46.0728 CenterY=-69.424 CenterZ=0 NormalX=0 NormalY=0 NormalZ=1 AngleXU=0 Radius=1
    g315: BSplineCurve PolesCount=3 KnotsCount=2 Degree=2 IsPeriodic=0
    g316: GeomPoint X=42.5666 Y=-67.3492 Z=0
    g317: GeomPoint X=46.0728 Y=-69.424 Z=0
    g318: Circle CenterX=46.0728 CenterY=-87.7794 CenterZ=0 NormalX=0 NormalY=0 NormalZ=1 AngleXU=0 Radius=1
    g319: Circle CenterX=46.0728 CenterY=-91.7794 CenterZ=0 NormalX=0 NormalY=0 NormalZ=1 AngleXU=0 Radius=1
    g320: Circle CenterX=42.0728 CenterY=-91.7794 CenterZ=0 NormalX=0 NormalY=0 NormalZ=1 AngleXU=0 Radius=1
    g321: BSplineCurve PolesCount=3 KnotsCount=2 Degree=2 IsPeriodic=0
    g322: GeomPoint X=46.0728 Y=-87.7794 Z=0
    g323: GeomPoint X=42.0728 Y=-91.7794 Z=0
    g324: Circle CenterX=2.07281 CenterY=-91.7794 CenterZ=0 NormalX=0 NormalY=0 NormalZ=1 AngleXU=0 Radius=1
    g325: Circle CenterX=-1.92719 CenterY=-91.7794 CenterZ=0 NormalX=0 NormalY=0 NormalZ=1 AngleXU=0 Radius=1
    g326: Circle CenterX=1.57905 CenterY=-89.8542 CenterZ=0 NormalX=0 NormalY=0 NormalZ=1 AngleXU=0 Radius=1
    g327: BSplineCurve PolesCount=3 KnotsCount=2 Degree=2 IsPeriodic=0
    g328: GeomPoint X=2.07281 Y=-91.7794 Z=0
    g329: GeomPoint X=1.57905 Y=-89.8542 Z=0
    g330: LineSegment StartX=2.07281 StartY=-91.7794 StartZ=0 EndX=42.0728 EndY=-91.7794 EndZ=0
    g331: LineSegment StartX=46.0728 StartY=-87.7794 StartZ=0 EndX=46.0728 EndY=-69.424 EndZ=0
    g332: LineSegment StartX=42.5666 StartY=-67.3492 StartZ=0 EndX=1.57905 EndY=-89.8542 EndZ=0
    g333: Circle CenterX=322.073 CenterY=76.4095 CenterZ=0 NormalX=0 NormalY=0 NormalZ=1 AngleXU=0 Radius=4
    g334: BSplineCurve PolesCount=3 KnotsCount=2 Degree=2 IsPeriodic=0
    g335: GeomPoint X=318.073 Y=72.4095 Z=0
    g336: GeomPoint X=322.073 Y=76.4095 Z=0
    g337: Circle CenterX=375.073 CenterY=72.4095 CenterZ=0 NormalX=0 NormalY=0 NormalZ=1 AngleXU=0 Radius=1
    g338: Circle CenterX=375.073 CenterY=76.4095 CenterZ=0 NormalX=0 NormalY=0 NormalZ=1 AngleXU=0 Radius=1
    g339: Circle CenterX=371.073 CenterY=76.4095 CenterZ=0 NormalX=0 NormalY=0 NormalZ=1 AngleXU=0 Radius=1
    g340: BSplineCurve PolesCount=3 KnotsCount=2 Degree=2 IsPeriodic=0
    g341: GeomPoint X=375.073 Y=72.4095 Z=0
    g342: GeomPoint X=371.073 Y=76.4095 Z=0
    g343: LineSegment StartX=322.073 StartY=76.4095 StartZ=0 EndX=371.073 EndY=76.4095 EndZ=0
    g344: LineSegment StartX=318.073 StartY=72.4095 StartZ=0 EndX=318.073 EndY=-47.4805 EndZ=0
    g345: LineSegment StartX=375.073 StartY=72.4095 StartZ=0 EndX=375.073 EndY=-78.7896 EndZ=0
    g346: ArcOfCircle CenterX=-26.9272 CenterY=22.1087 CenterZ=0 NormalX=0 NormalY=0 NormalZ=1 AngleXU=0 Radius=4 StartAngle=5e-16 EndAngle=3.14159
    g347: LineSegment StartX=-30.9272 StartY=22.1087 StartZ=0 EndX=-34.9272 EndY=-83.7794 EndZ=0
    g348: LineSegment StartX=-18.9272 StartY=-83.7794 StartZ=0 EndX=-22.9272 EndY=22.1087 EndZ=0
  constraints (572):
    c: Coincident(g0,g2)
    c: Block(g0)
    c: Block(g1)
    c: Vertical(g3)
    c: Vertical(g4)
    c: Block(g4)
    c: Block(g3)
    c: Tangent(g6,g7) = 1.5708
    c: Tangent(g7,g9) = 1.5708
    c: Equal(g6,g9)
    c: Coincident(g8,g6)
    c: Coincident(g8,g9)
    c: Block(g7)
    c: Block(g8)
    c: Weight(g10) = 1
    c: Equal(g10,g11)
    c: Equal(g10,g12)
    c: InternalAlignment(g10,g13)
    c: InternalAlignment(g11,g13)
    c: InternalAlignment(g12,g13)
    c: InternalAlignment(g14,g13)
    c: InternalAlignment(g15,g13)
    c: Weight(g16) = 1
    c: Equal(g16,g17)
    c: Equal(g16,g18)
    c: InternalAlignment(g16,g19)
    c: InternalAlignment(g17,g19)
    c: InternalAlignment(g18,g19)
    c: InternalAlignment(g20,g19)
    c: InternalAlignment(g21,g19)
    c: Block(g19)
    c: Block(g13)
    c: Weight(g22) = 1
    c: Equal(g22,g23)
    c: Equal(g22,g24)
    c: InternalAlignment(g22,g25)
    c: InternalAlignment(g23,g25)
    c: InternalAlignment(g24,g25)
    c: InternalAlignment(g26,g25)
    c: InternalAlignment(g27,g25)
    c: Weight(g28) = 1
    c: Equal(g28,g29)
    c: Equal(g28,g30)
    c: InternalAlignment(g28,g31)
    c: InternalAlignment(g29,g31)
    c: InternalAlignment(g30,g31)
    c: InternalAlignment(g32,g31)
    c: InternalAlignment(g33,g31)
    c: Block(g31)
    c: Block(g25)
    c: Weight(g34) = 1
    c: Equal(g34,g35)
    c: Equal(g34,g36)
    c: InternalAlignment(g34,g37)
    c: InternalAlignment(g35,g37)
    c: InternalAlignment(g36,g37)
    c: InternalAlignment(g38,g37)
    c: InternalAlignment(g39,g37)
    c: Weight(g40) = 1
    c: Equal(g40,g41)
    c: Equal(g40,g42)
    c: InternalAlignment(g40,g43)
    c: InternalAlignment(g41,g43)
    c: InternalAlignment(g42,g43)
    c: InternalAlignment(g44,g43)
    c: InternalAlignment(g45,g43)
    c: Block(g37)
    c: Block(g43)
    c: Coincident(g46,g4)
    c: Coincident(g46,g3)
    c: Horizontal(g46)
    c: Distance(g46) = 450
    c: Coincident(g47,g4)
    c: Coincident(g47,g3)
    c: Horizontal(g47)
    c: Horizontal(g48)
    c: Coincident(g2,g48)
    c: Block(g48)
    c: Coincident(g1,g48)
    c: Weight(g49) = 1
    c: Equal(g49,g50)
    c: Equal(g49,g51)
    c: InternalAlignment(g49,g52)
    c: InternalAlignment(g50,g52)
    c: InternalAlignment(g51,g52)
    c: InternalAlignment(g53,g52)
    c: InternalAlignment(g54,g52)
    c: Block(g52)
    c: Weight(g55) = 1
    c: Equal(g55,g56)
    c: Equal(g55,g57)
    c: InternalAlignment(g55,g58)
    c: InternalAlignment(g56,g58)
    c: InternalAlignment(g57,g58)
    c: InternalAlignment(g59,g58)
    c: InternalAlignment(g60,g58)
    c: Block(g58)
    c: Weight(g61) = 1
    c: Equal(g61,g62)
    c: Equal(g61,g63)
    c: InternalAlignment(g61,g64)
    c: InternalAlignment(g62,g64)
    c: InternalAlignment(g63,g64)
    c: InternalAlignment(g65,g64)
    c: InternalAlignment(g66,g64)
    c: Block(g64)
    c: Weight(g67) = 1
    c: Equal(g67,g68)
    c: Equal(g67,g69)
    c: InternalAlignment(g67,g70)
    c: InternalAlignment(g68,g70)
    c: InternalAlignment(g69,g70)
    c: InternalAlignment(g71,g70)
    c: InternalAlignment(g72,g70)
    c: Block(g70)
    c: Weight(g73) = 1
    c: Equal(g73,g74)
    c: Equal(g73,g75)
    c: InternalAlignment(g73,g76)
    c: InternalAlignment(g74,g76)
    c: InternalAlignment(g75,g76)
    c: InternalAlignment(g77,g76)
    c: InternalAlignment(g78,g76)
    c: Weight(g79) = 1
    c: Equal(g79,g80)
    c: Equal(g79,g81)
    c: InternalAlignment(g79,g82)
    c: InternalAlignment(g80,g82)
    c: InternalAlignment(g81,g82)
    c: InternalAlignment(g83,g82)
    c: InternalAlignment(g84,g82)
    c: Block(g76)
    c: Block(g82)
    c: Coincident(g85,g76)
    c: Coincident(g85,g82)
    c: Vertical(g85)
    c: Coincident(g86,g76)
    c: Coincident(g86,g58)
    c: Coincident(g87,g58)
    c: Coincident(g87,g82)
    c: Weight(g88) = 1
    c: Equal(g88,g89)
    c: Equal(g88,g90)
    c: InternalAlignment(g88,g91)
    c: InternalAlignment(g89,g91)
    c: InternalAlignment(g90,g91)
    c: InternalAlignment(g92,g91)
    c: InternalAlignment(g93,g91)
    c: Weight(g94) = 1
    c: Equal(g94,g95)
    c: Equal(g94,g96)
    c: InternalAlignment(g94,g97)
    c: InternalAlignment(g95,g97)
    c: InternalAlignment(g96,g97)
    c: InternalAlignment(g98,g97)
    c: InternalAlignment(g99,g97)
    c: Block(g91)
    c: Block(g97)
    c: Coincident(g100,g91)
    c: Coincident(g100,g97)
    c: Vertical(g100)
    c: Coincident(g101,g91)
    c: Coincident(g101,g52)
    c: Coincident(g102,g52)
    c: Coincident(g102,g97)
    c: Weight(g103) = 1
    c: Equal(g103,g104)
    c: Equal(g103,g105)
    c: InternalAlignment(g103,g106)
    c: InternalAlignment(g104,g106)
    c: InternalAlignment(g105,g106)
    c: InternalAlignment(g107,g106)
    c: InternalAlignment(g108,g106)
    c: Weight(g109) = 1
    c: Equal(g109,g110)
    c: Equal(g109,g111)
    c: InternalAlignment(g109,g112)
    c: InternalAlignment(g110,g112)
    c: InternalAlignment(g111,g112)
    c: InternalAlignment(g113,g112)
    c: InternalAlignment(g114,g112)
    c: Block(g106)
    c: Block(g112)
    c: Coincident(g115,g106)
    c: Coincident(g115,g112)
    c: Vertical(g115)
    c: Coincident(g116,g112)
    c: Coincident(g116,g70)
    c: Coincident(g117,g70)
    c: Coincident(g117,g106)
    c: Weight(g118) = 1
    c: Equal(g118,g119)
    c: Equal(g118,g120)
    c: InternalAlignment(g118,g121)
    c: InternalAlignment(g119,g121)
    c: InternalAlignment(g120,g121)
    c: InternalAlignment(g122,g121)
    c: InternalAlignment(g123,g121)
    c: Weight(g124) = 1
    c: Equal(g124,g125)
    c: Equal(g124,g126)
    c: InternalAlignment(g124,g127)
    c: InternalAlignment(g125,g127)
    c: InternalAlignment(g126,g127)
    c: InternalAlignment(g128,g127)
    c: InternalAlignment(g129,g127)
    c: Block(g121)
    c: Block(g127)
    c: Coincident(g130,g121)
    c: Coincident(g130,g127)
    c: Vertical(g130)
    c: Coincident(g131,g127)
    c: Coincident(g131,g64)
    c: Coincident(g132,g64)
    c: Coincident(g132,g121)
    c: Weight(g133) = 1
    c: Equal(g133,g134)
    c: Equal(g133,g135)
    c: InternalAlignment(g133,g136)
    c: InternalAlignment(g134,g136)
    c: InternalAlignment(g135,g136)
    c: InternalAlignment(g137,g136)
    c: InternalAlignment(g138,g136)
    c: Weight(g139) = 1
    c: Equal(g139,g140)
    c: Equal(g139,g141)
    c: InternalAlignment(g139,g142)
    c: InternalAlignment(g140,g142)
    c: InternalAlignment(g141,g142)
    c: InternalAlignment(g143,g142)
    c: InternalAlignment(g144,g142)
    c: Weight(g145) = 1
    c: Equal(g145,g146)
    c: Equal(g145,g147)
    c: InternalAlignment(g145,g148)
    c: InternalAlignment(g146,g148)
    c: InternalAlignment(g147,g148)
    c: InternalAlignment(g149,g148)
    c: InternalAlignment(g150,g148)
    c: Weight(g151) = 1
    c: Equal(g151,g152)
    c: Equal(g151,g153)
    c: InternalAlignment(g151,g154)
    c: InternalAlignment(g152,g154)
    c: InternalAlignment(g153,g154)
    c: InternalAlignment(g155,g154)
    c: InternalAlignment(g156,g154)
    c: Block(g154)
    c: Block(g148)
    c: Block(g142)
    c: Block(g136)
    c: Coincident(g157,g31)
    c: Coincident(g157,g154)
    c: Coincident(g158,g154)
    c: Coincident(g158,g148)
    c: Horizontal(g158)
    c: Coincident(g159,g148)
    c: Coincident(g159,g31)
    c: Vertical(g159)
    c: Coincident(g160,g25)
    c: Coincident(g160,g142)
    c: Vertical(g160)
    c: Coincident(g161,g142)
    c: Coincident(g161,g136)
    c: Horizontal(g161)
    c: Coincident(g162,g136)
    c: Coincident(g162,g25)
    c: Weight(g163) = 1
    c: Equal(g163,g164)
    c: Equal(g163,g165)
    c: InternalAlignment(g163,g166)
    c: InternalAlignment(g164,g166)
    c: InternalAlignment(g165,g166)
    c: InternalAlignment(g167,g166)
    c: InternalAlignment(g168,g166)
    c: Weight(g169) = 1
    c: Equal(g169,g170)
    c: Equal(g169,g171)
    c: InternalAlignment(g169,g172)
    c: InternalAlignment(g170,g172)
    c: InternalAlignment(g171,g172)
    c: InternalAlignment(g173,g172)
    c: InternalAlignment(g174,g172)
    c: Weight(g175) = 1
    c: Equal(g175,g176)
    c: Equal(g175,g177)
    c: InternalAlignment(g175,g178)
    c: InternalAlignment(g176,g178)
    c: InternalAlignment(g177,g178)
    c: InternalAlignment(g179,g178)
    c: InternalAlignment(g180,g178)
    c: Weight(g181) = 1
    c: Equal(g181,g182)
    c: Equal(g181,g183)
    c: InternalAlignment(g181,g184)
    c: InternalAlignment(g182,g184)
    c: InternalAlignment(g183,g184)
    c: InternalAlignment(g185,g184)
    c: InternalAlignment(g186,g184)
    c: Block(g184)
    c: Block(g178)
    c: Block(g172)
    c: Block(g166)
    c: Coincident(g187,g184)
    c: Coincident(g187,g178)
    c: Horizontal(g187)
    c: Coincident(g188,g178)
    c: Coincident(g188,g13)
    c: Vertical(g188)
    c: Coincident(g189,g19)
    c: Coincident(g189,g172)
    c: Vertical(g189)
    c: Coincident(g190,g172)
    c: Coincident(g190,g166)
    c: Horizontal(g190)
    c: Coincident(g191,g166)
    c: Coincident(g191,g19)
    c: Coincident(g192,g13)
    c: Weight(g193) = 1
    c: Equal(g193,g194)
    c: Equal(g193,g195)
    c: InternalAlignment(g193,g196)
    c: InternalAlignment(g194,g196)
    c: InternalAlignment(g195,g196)
    c: InternalAlignment(g197,g196)
    c: InternalAlignment(g198,g196)
    c: Weight(g199) = 1
    c: Equal(g199,g200)
    c: Equal(g199,g201)
    c: InternalAlignment(g199,g202)
    c: InternalAlignment(g200,g202)
    c: InternalAlignment(g201,g202)
    c: InternalAlignment(g203,g202)
    c: InternalAlignment(g204,g202)
    c: Block(g202)
    c: Block(g196)
    c: Coincident(g205,g202)
    c: Coincident(g205,g37)
    c: Coincident(g206,g37)
    c: Coincident(g206,g196)
    c: Coincident(g207,g196)
    c: Coincident(g207,g202)
    c: Vertical(g207)
    c: Weight(g208) = 1
    c: Equal(g208,g209)
    c: Equal(g208,g210)
    c: InternalAlignment(g208,g211)
    c: InternalAlignment(g209,g211)
    c: InternalAlignment(g210,g211)
    c: InternalAlignment(g212,g211)
    c: InternalAlignment(g213,g211)
    c: Weight(g214) = 1
    c: Equal(g214,g215)
    c: Equal(g214,g216)
    c: InternalAlignment(g214,g217)
    c: InternalAlignment(g215,g217)
    c: InternalAlignment(g216,g217)
    c: InternalAlignment(g218,g217)
    c: InternalAlignment(g219,g217)
    c: Block(g217)
    c: Block(g211)
    c: Coincident(g220,g211)
    c: Coincident(g220,g43)
    c: Coincident(g221,g43)
    c: Coincident(g221,g217)
    c: Coincident(g222,g217)
    c: Coincident(g222,g211)
    c: Vertical(g222)
    c: Horizontal(g223)
    c: Block(g223)
    c: Vertical(g224)
    c: Block(g224)
    c: Block(g225)
    c: Weight(g226) = 1
    c: Equal(g226,g227)
    c: Equal(g226,g228)
    c: InternalAlignment(g226,g229)
    c: InternalAlignment(g227,g229)
    c: InternalAlignment(g228,g229)
    c: InternalAlignment(g230,g229)
    c: InternalAlignment(g231,g229)
    c: Weight(g232) = 1
    c: Equal(g232,g233)
    c: Equal(g232,g234)
    c: InternalAlignment(g232,g235)
    c: InternalAlignment(g233,g235)
    c: InternalAlignment(g234,g235)
    c: InternalAlignment(g236,g235)
    c: InternalAlignment(g237,g235)
    c: Weight(g238) = 1
    c: Equal(g238,g239)
    c: Equal(g238,g240)
    c: InternalAlignment(g238,g241)
    c: InternalAlignment(g239,g241)
    c: InternalAlignment(g240,g241)
    c: InternalAlignment(g242,g241)
    c: InternalAlignment(g243,g241)
    c: Weight(g244) = 1
    c: Equal(g244,g245)
    c: Equal(g244,g246)
    c: InternalAlignment(g244,g247)
    c: InternalAlignment(g245,g247)
    c: InternalAlignment(g246,g247)
    c: InternalAlignment(g248,g247)
    c: InternalAlignment(g249,g247)
    c: Block(g229)
    c: Block(g235)
    c: Block(g241)
    c: Block(g247)
    c: Coincident(g250,g235)
    c: Coincident(g250,g229)
    c: Horizontal(g250)
    c: Block(g192)
    c: Weight(g251) = 1
    c: Equal(g251,g252)
    c: Equal(g251,g253)
    c: InternalAlignment(g251,g254)
    c: InternalAlignment(g252,g254)
    c: InternalAlignment(g253,g254)
    c: InternalAlignment(g255,g254)
    c: InternalAlignment(g256,g254)
    c: Weight(g257) = 1
    c: Equal(g257,g258)
    c: Equal(g257,g259)
    c: InternalAlignment(g257,g260)
    c: InternalAlignment(g258,g260)
    c: InternalAlignment(g259,g260)
    c: InternalAlignment(g261,g260)
    c: InternalAlignment(g262,g260)
    c: Block(g254)
    c: Block(g260)
    c: Coincident(g263,g254)
    c: Coincident(g263,g260)
    c: Weight(g264) = 1
    c: Equal(g264,g265)
    c: Equal(g264,g266)
    c: InternalAlignment(g264,g267)
    c: InternalAlignment(g265,g267)
    c: InternalAlignment(g266,g267)
    c: InternalAlignment(g268,g267)
    c: InternalAlignment(g269,g267)
    c: Weight(g270) = 1
    c: Equal(g270,g271)
    c: Equal(g270,g272)
    c: InternalAlignment(g270,g273)
    c: InternalAlignment(g271,g273)
    c: InternalAlignment(g272,g273)
    c: InternalAlignment(g274,g273)
    c: InternalAlignment(g275,g273)
    c: Weight(g276) = 1
    c: Equal(g276,g277)
    c: Equal(g276,g278)
    c: InternalAlignment(g276,g279)
    c: InternalAlignment(g277,g279)
    c: InternalAlignment(g278,g279)
    c: InternalAlignment(g280,g279)
    c: InternalAlignment(g281,g279)
    c: Block(g279)
    c: Block(g273)
    c: Block(g267)
    c: Coincident(g282,g273)
    c: Coincident(g282,g267)
    c: Coincident(g283,g267)
    c: Coincident(g283,g279)
    c: Vertical(g283)
    c: Coincident(g284,g279)
    c: Coincident(g284,g273)
    c: Horizontal(g284)
    c: Weight(g285) = 1
    c: Equal(g285,g286)
    c: InternalAlignment(g285,g287)
    c: InternalAlignment(g286,g287)
    c: InternalAlignment(g288,g287)
    c: InternalAlignment(g289,g287)
    c: Weight(g290) = 1
    c: InternalAlignment(g291,g293)
    c: InternalAlignment(g292,g293)
    c: InternalAlignment(g294,g293)
    c: InternalAlignment(g295,g293)
    c: Weight(g296) = 1
    c: Equal(g296,g297)
    c: Equal(g296,g298)
    c: InternalAlignment(g296,g299)
    c: InternalAlignment(g297,g299)
    c: InternalAlignment(g298,g299)
    c: InternalAlignment(g300,g299)
    c: InternalAlignment(g301,g299)
    c: Equal(g302,g303)
    c: Equal(g302,g304)
    c: InternalAlignment(g302,g305)
    c: InternalAlignment(g303,g305)
    c: InternalAlignment(g304,g305)
    c: InternalAlignment(g306,g305)
    c: InternalAlignment(g307,g305)
    c: Block(g293)
    c: Block(g299)
    c: Block(g305)
    c: Block(g287)
    c: Coincident(g308,g287)
    c: Coincident(g308,g293)
    c: Horizontal(g308)
    c: Coincident(g309,g293)
    c: Coincident(g309,g299)
    c: Vertical(g309)
    c: Coincident(g310,g299)
    c: Coincident(g310,g305)
    c: Horizontal(g310)
    c: Coincident(g311,g305)
    c: Coincident(g311,g287)
    c: Weight(g312) = 1
    c: Equal(g312,g313)
    c: Equal(g312,g314)
    c: InternalAlignment(g312,g315)
    c: InternalAlignment(g313,g315)
    c: InternalAlignment(g314,g315)
    c: InternalAlignment(g316,g315)
    c: InternalAlignment(g317,g315)
    c: Weight(g318) = 1
    c: Equal(g318,g319)
    c: Equal(g318,g320)
    c: InternalAlignment(g318,g321)
    c: InternalAlignment(g319,g321)
    c: InternalAlignment(g320,g321)
    c: InternalAlignment(g322,g321)
    c: InternalAlignment(g323,g321)
    c: Weight(g324) = 1
    c: Equal(g324,g325)
    c: Equal(g324,g326)
    c: InternalAlignment(g324,g327)
    c: InternalAlignment(g325,g327)
    c: InternalAlignment(g326,g327)
    c: InternalAlignment(g328,g327)
    c: InternalAlignment(g329,g327)
    c: Block(g327)
    c: Block(g321)
    c: Block(g315)
    c: Coincident(g330,g327)
    c: Coincident(g330,g321)
    c: Horizontal(g330)
    c: Coincident(g331,g321)
    c: Coincident(g331,g315)
    c: Vertical(g331)
    c: Coincident(g332,g315)
    c: Coincident(g332,g327)
    c: InternalAlignment(g333,g334)
    c: InternalAlignment(g335,g334)
    c: InternalAlignment(g336,g334)
    c: Block(g334)
    c: Equal(g337,g338)
    c: Equal(g337,g339)
    c: InternalAlignment(g337,g340)
    c: InternalAlignment(g338,g340)
    c: InternalAlignment(g339,g340)
    c: InternalAlignment(g341,g340)
    c: InternalAlignment(g342,g340)
    c: Block(g340)
    c: Coincident(g343,g334)
    c: Horizontal(g343)
    c: Block(g343)
    c: Coincident(g344,g334)
    c: Coincident(g344,g260)
    c: Vertical(g344)
    c: Coincident(g345,g340)
    c: Coincident(g345,g254)
    c: Vertical(g345)
    c: Coincident(g347,g5)
    c: Coincident(g348,g5)
    c: Block(g346)
    c: Block(g5)
    c: Block(g348)
    c: Block(g347)
    c: Distance(g344) = 119.89
FEATURE [Sketcher::SketchObject] Sketch001
  FullyConstrained = true
  MapMode = 4
  Placement = pos=(0,0,0) rot=(0.57735,0.57735,0.57735;2.0944rad)
  Support = -> [Sketch]
  sketch-geometry (46):
    g0: BSplineCurve PolesCount=3 KnotsCount=2 Degree=2 IsPeriodic=0
    g1: ArcOfCircle CenterX=73.1223 CenterY=-32.291 CenterZ=0 NormalX=0 NormalY=0 NormalZ=1 AngleXU=0 Radius=13 StartAngle=5.92268 EndAngle=9.06428
    g2: ArcOfCircle CenterX=66.7816 CenterY=-49.1439 CenterZ=0 NormalX=0 NormalY=0 NormalZ=1 AngleXU=0 Radius=13 StartAngle=2.78068 EndAngle=5.92131
    g3: ArcOfCircle CenterX=55.9263 CenterY=-78.1807 CenterZ=0 NormalX=0 NormalY=0 NormalZ=1 AngleXU=0 Radius=13 StartAngle=5.92268 EndAngle=9.06428
    g4: ArcOfCircle CenterX=49.5884 CenterY=-95.0342 CenterZ=0 NormalX=0 NormalY=0 NormalZ=1 AngleXU=0 Radius=13 StartAngle=2.78068 EndAngle=5.92131
    g5: ArcOfCircle CenterX=38.7206 CenterY=-124.067 CenterZ=0 NormalX=0 NormalY=0 NormalZ=1 AngleXU=0 Radius=13 StartAngle=5.92268 EndAngle=9.06428
    g6: ArcOfCircle CenterX=32.3875 CenterY=-140.92 CenterZ=0 NormalX=0 NormalY=0 NormalZ=1 AngleXU=0 Radius=13 StartAngle=2.78068 EndAngle=5.92131
    g7: ArcOfCircle CenterX=21.4715 CenterY=-169.934 CenterZ=0 NormalX=0 NormalY=0 NormalZ=1 AngleXU=0 Radius=13 StartAngle=5.92268 EndAngle=9.06428
    g8: ArcOfCircle CenterX=15.1336 CenterY=-186.787 CenterZ=0 NormalX=0 NormalY=0 NormalZ=1 AngleXU=0 Radius=13 StartAngle=2.78068 EndAngle=5.92131
    g9-g12: Circle x4 (B-spline internal-alignment scaffolding for g13; pole/knot coordinates omitted)
    g13: BSplineCurve PolesCount=4 KnotsCount=2 Degree=3 IsPeriodic=0
    g14: GeomPoint X=28.8094 Y=-19.0875 Z=0
    g15: GeomPoint X=47.0443 Y=-50.4712 Z=0
    g16: Circle CenterX=53.5586 CenterY=-23.2695 CenterZ=0 NormalX=0 NormalY=0 NormalZ=1 AngleXU=0 Radius=3.24518
    g17: Circle CenterX=-195.441 CenterY=-127.082 CenterZ=0 NormalX=0 NormalY=0 NormalZ=1 AngleXU=0 Radius=1
    g18: Circle CenterX=-8.24091 CenterY=-197.481 CenterZ=0 NormalX=0 NormalY=0 NormalZ=1 AngleXU=0 Radius=1
    g19: Circle CenterX=12.8789 CenterY=-141.321 CenterZ=0 NormalX=0 NormalY=0 NormalZ=1 AngleXU=0 Radius=1
    g20: BSplineCurve PolesCount=3 KnotsCount=2 Degree=2 IsPeriodic=0
    g21: GeomPoint X=-195.441 Y=-127.082 Z=0
    g22: GeomPoint X=12.8789 Y=-141.321 Z=0
    g23: Circle CenterX=-12.8016 CenterY=-179.036 CenterZ=0 NormalX=0 NormalY=0 NormalZ=1 AngleXU=0 Radius=10.5072
    g24: Circle CenterX=0.933922 CenterY=-166.43 CenterZ=0 NormalX=0 NormalY=0 NormalZ=1 AngleXU=0 Radius=3.26661
    g25: Circle CenterX=-33.5518 CenterY=-176.44 CenterZ=0 NormalX=0 NormalY=0 NormalZ=1 AngleXU=0 Radius=5.64388
    g26: Circle CenterX=-47.2366 CenterY=-173.859 CenterZ=0 NormalX=0 NormalY=0 NormalZ=1 AngleXU=0 Radius=3.01653
    g27: Circle CenterX=-56.2595 CenterY=-171.456 CenterZ=0 NormalX=0 NormalY=0 NormalZ=1 AngleXU=0 Radius=2.12826
    g28: ArcOfCircle CenterX=51.2151 CenterY=-198.473 CenterZ=0 NormalX=0 NormalY=0 NormalZ=1 AngleXU=0 Radius=20 StartAngle=2.78189 EndAngle=4.35269
    g29: LineSegment StartX=32.4951 StartY=-191.433 StartZ=0 EndX=94.6578 EndY=-26.1352 EndZ=0
    g30: LineSegment StartX=43.1192 StartY=-220.001 StartZ=0 EndX=-196.497 EndY=-129.89 EndZ=0
    g31: LineSegment StartX=43.1192 StartY=-220.001 StartZ=0 EndX=44.1752 EndY=-217.193 EndZ=0
    g32: LineSegment StartX=117.223 StartY=-19.0875 StartZ=0 EndX=117.223 EndY=-16.0875 EndZ=0
    g33: LineSegment StartX=117.223 StartY=-16.0875 StartZ=0 EndX=17.2232 EndY=-16.0875 EndZ=0
    g34: LineSegment StartX=17.2232 StartY=-16.0875 StartZ=0 EndX=17.2232 EndY=-19.0875 EndZ=0
    g35: LineSegment StartX=28.8094 StartY=-19.0875 StartZ=0 EndX=17.2232 EndY=-19.0875 EndZ=0
    g36: LineSegment StartX=47.0443 StartY=-50.4712 StartZ=0 EndX=12.8789 EndY=-141.321 EndZ=0
    g37: LineSegment StartX=-195.441 StartY=-127.082 StartZ=0 EndX=-196.497 EndY=-129.89 EndZ=0
    g38: LineSegment StartX=85.2866 StartY=-36.8766 StartZ=0 EndX=78.9396 EndY=-53.7463 EndZ=0
    g39: LineSegment StartX=60.9579 StartY=-27.7053 StartZ=0 EndX=54.6191 EndY=-44.5532 EndZ=0
    g40: LineSegment StartX=68.0907 StartY=-82.7664 StartZ=0 EndX=61.7465 EndY=-99.6365 EndZ=0
    g41: LineSegment StartX=43.7619 StartY=-73.595 StartZ=0 EndX=37.426 EndY=-90.4435 EndZ=0
    g42: LineSegment StartX=50.885 StartY=-128.652 StartZ=0 EndX=44.5456 EndY=-145.522 EndZ=0
    g43: LineSegment StartX=26.5562 StartY=-119.481 StartZ=0 EndX=20.2251 EndY=-136.329 EndZ=0
    g44: LineSegment StartX=9.3071 StartY=-165.349 StartZ=0 EndX=2.97115 EndY=-182.197 EndZ=0
    g45: LineSegment StartX=33.6358 StartY=-174.52 StartZ=0 EndX=27.2917 EndY=-191.39 EndZ=0
  constraints (71):
    c: Block(g0)
    c: Block(g1)
    c: Block(g2)
    c: Block(g4)
    c: Block(g3)
    c: Block(g6)
    c: Block(g5)
    c: Block(g8)
    c: Block(g7)
    c: Weight(g9) = 1
    c: Equal(g9,g10)
    c: Equal(g9,g11)
    c: Equal(g9,g12)
    c: InternalAlignment(g9-g12 -> g13) x4
    c: InternalAlignment(g14,g13)
    c: InternalAlignment(g15,g13)
    c: Block(g16)
    c: Weight(g17) = 1
    c: Equal(g17,g18)
    c: Equal(g17,g19)
    c: InternalAlignment(g17,g20)
    c: InternalAlignment(g18,g20)
    c: InternalAlignment(g19,g20)
    c: InternalAlignment(g21,g20)
    c: InternalAlignment(g22,g20)
    c: Block(g20)
    c: Block(g23)
    c: Block(g24)
    c: Block(g25)
    c: Block(g26)
    c: Block(g27)
    c: Block(g28)
    c: Coincident(g29,g28)
    c: Coincident(g29,g0)
    c: Block(g13)
    c: Coincident(g31,g30)
    c: Coincident(g31,g28)
    c: Block(g31)
    c: Coincident(g32,g0)
    c: Vertical(g32)
    c: Coincident(g33,g32)
    c: Horizontal(g33)
    c: Coincident(g34,g33)
    c: Vertical(g34)
    c: Block(g33)
    c: Coincident(g35,g13)
    c: Coincident(g35,g34)
    c: Horizontal(g35)
    c: Coincident(g36,g13)
    c: Coincident(g36,g20)
    c: Coincident(g37,g20)
    c: Coincident(g37,g30)
    c: Block(g30)
    c: Coincident(g38,g1)
    c: Coincident(g38,g2)
    c: Coincident(g39,g1)
    c: Coincident(g39,g2)
    c: Coincident(g40,g3)
    c: Coincident(g40,g4)
    c: Coincident(g41,g3)
    c: Coincident(g41,g4)
    c: Coincident(g42,g5)
    c: Coincident(g42,g6)
    c: Coincident(g43,g5)
    c: Coincident(g43,g6)
    c: Coincident(g44,g7)
    c: Coincident(g44,g8)
    c: Coincident(g45,g7)
    c: Coincident(g45,g8)
    c: Distance(g30) = 256
    c: Distance(g33) = 100
FEATURE [Part::Extrusion] Extrude002
  Base = -> Sketch001
  Dir = (1,0,0)
  DirMode = 2
  FaceMakerClass = Part::FaceMakerBullseye
  LengthFwd = 8
  LengthRev = 0
  Solid = true
  Symmetric = false
FEATURE [Sketcher::SketchObject] Sketch002
  FullyConstrained = true
  sketch-geometry (20):
    g0: LineSegment StartX=-2.77179 StartY=-200.304 StartZ=0 EndX=5.22821 EndY=-200.304 EndZ=0
    g1: LineSegment StartX=5.22821 StartY=-200.304 StartZ=0 EndX=5.22821 EndY=-197.304 EndZ=0
    g2: LineSegment StartX=-2.77179 StartY=-200.304 StartZ=0 EndX=-2.77179 EndY=-197.304 EndZ=0
    g3: LineSegment StartX=5.22821 StartY=-197.304 StartZ=0 EndX=8.22821 EndY=-197.304 EndZ=0
    g4: LineSegment StartX=-2.77179 StartY=-197.304 StartZ=0 EndX=-5.77179 EndY=-197.304 EndZ=0
    g5: LineSegment StartX=19.2282 StartY=-203.304 StartZ=0 EndX=19.2282 EndY=-206.304 EndZ=0
    g6: LineSegment StartX=-16.7718 StartY=-203.304 StartZ=0 EndX=-16.7718 EndY=-206.304 EndZ=0
    g7: LineSegment StartX=-16.7718 StartY=-206.304 StartZ=0 EndX=19.2282 EndY=-206.304 EndZ=0
    g8: Circle CenterX=-16.7718 CenterY=-203.304 CenterZ=0 NormalX=0 NormalY=0 NormalZ=1 AngleXU=0 Radius=1
    g9: Circle CenterX=-5.77179 CenterY=-203.304 CenterZ=0 NormalX=0 NormalY=0 NormalZ=1 AngleXU=0 Radius=1
    g10: Circle CenterX=-5.77179 CenterY=-197.304 CenterZ=0 NormalX=0 NormalY=0 NormalZ=1 AngleXU=0 Radius=1
    g11: BSplineCurve PolesCount=3 KnotsCount=2 Degree=2 IsPeriodic=0
    g12: GeomPoint X=-16.7718 Y=-203.304 Z=0
    g13: GeomPoint X=-5.77179 Y=-197.304 Z=0
    g14: Circle CenterX=19.2282 CenterY=-203.304 CenterZ=0 NormalX=0 NormalY=0 NormalZ=1 AngleXU=0 Radius=1
    g15: Circle CenterX=8.22821 CenterY=-203.304 CenterZ=0 NormalX=0 NormalY=0 NormalZ=1 AngleXU=0 Radius=1
    g16: Circle CenterX=8.22821 CenterY=-197.304 CenterZ=0 NormalX=0 NormalY=0 NormalZ=1 AngleXU=0 Radius=1
    g17: BSplineCurve PolesCount=3 KnotsCount=2 Degree=2 IsPeriodic=0
    g18: GeomPoint X=19.2282 Y=-203.304 Z=0
    g19: GeomPoint X=8.22821 Y=-197.304 Z=0
  constraints (41):
    c: Horizontal(g0)
    c: Distance(g0) = 8
    c: Coincident(g1,g0)
    c: Vertical(g1)
    c: Distance(g1) = 3
    c: Coincident(g2,g0)
    c: Vertical(g2)
    c: Distance(g2) = 3
    c: Coincident(g3,g1)
    c: Horizontal(g3)
    c: Distance(g3) = 3
    c: Coincident(g4,g2)
    c: Horizontal(g4)
    c: Distance(g4) = 3
    c: Vertical(g5)
    c: Vertical(g6)
    c: Coincident(g7,g6)
    c: Coincident(g7,g5)
    c: Weight(g8) = 1
    c: Equal(g8,g9)
    c: Equal(g8,g10)
    c: Coincident(g11,g4)
    c: InternalAlignment(g8,g11)
    c: InternalAlignment(g9,g11)
    c: InternalAlignment(g10,g11)
    c: InternalAlignment(g12,g11)
    c: InternalAlignment(g13,g11)
    c: Coincident(g17,g5)
    c: Weight(g14) = 1
    c: Equal(g14,g15)
    c: Equal(g14,g16)
    c: Coincident(g17,g3)
    c: InternalAlignment(g14,g17)
    c: InternalAlignment(g15,g17)
    c: InternalAlignment(g16,g17)
    c: InternalAlignment(g18,g17)
    c: InternalAlignment(g19,g17)
    c: Block(g7)
    c: Block(g17)
    c: Block(g11)
    c: Block(g6)
FEATURE [Part::Extrusion] Extrude003
  Base = -> Sketch002
  Dir = (0,0,1)
  DirMode = 2
  FaceMakerClass = Part::FaceMakerBullseye
  LengthFwd = 260
  LengthRev = 0
  Solid = true
  Symmetric = false
FEATURE [Sketcher::SketchObject] Sketch003
  FullyConstrained = false
  sketch-geometry (378):
    g0: LineSegment StartX=-42.9272 StartY=136.221 StartZ=0 EndX=-42.9272 EndY=-103.779 EndZ=0
    g1: LineSegment StartX=407.073 StartY=136.221 StartZ=0 EndX=407.073 EndY=-103.779 EndZ=0
    g2: ArcOfCircle CenterX=-26.9272 CenterY=-83.7794 CenterZ=0 NormalX=0 NormalY=0 NormalZ=1 AngleXU=0 Radius=8 StartAngle=3.14159 EndAngle=6.28319
    g3: ArcOfCircle CenterX=391.073 CenterY=-83.7794 CenterZ=0 NormalX=0 NormalY=0 NormalZ=1 AngleXU=0 Radius=8 StartAngle=3.14159 EndAngle=6.28319
    g4: Circle CenterX=175.022 CenterY=27.0628 CenterZ=0 NormalX=0 NormalY=0 NormalZ=1 AngleXU=0 Radius=1
    g5: Circle CenterX=179.022 CenterY=24.8665 CenterZ=0 NormalX=0 NormalY=0 NormalZ=1 AngleXU=0 Radius=1
    g6: Circle CenterX=179.022 CenterY=27.0628 CenterZ=0 NormalX=0 NormalY=0 NormalZ=1 AngleXU=0 Radius=1
    g7: BSplineCurve PolesCount=3 KnotsCount=2 Degree=2 IsPeriodic=0
    g8: GeomPoint X=175.022 Y=27.0628 Z=0
    g9: GeomPoint X=179.022 Y=27.0628 Z=0
    g10: Circle CenterX=189.124 CenterY=27.0628 CenterZ=0 NormalX=0 NormalY=0 NormalZ=1 AngleXU=0 Radius=1
    g11: Circle CenterX=185.124 CenterY=24.8665 CenterZ=0 NormalX=0 NormalY=0 NormalZ=1 AngleXU=0 Radius=1
    g12: Circle CenterX=185.124 CenterY=27.0628 CenterZ=0 NormalX=0 NormalY=0 NormalZ=1 AngleXU=0 Radius=1
    g13: BSplineCurve PolesCount=3 KnotsCount=2 Degree=2 IsPeriodic=0
    g14: GeomPoint X=189.124 Y=27.0628 Z=0
    g15: GeomPoint X=185.124 Y=27.0628 Z=0
    g16: Circle CenterX=175.022 CenterY=5.37834 CenterZ=0 NormalX=0 NormalY=0 NormalZ=1 AngleXU=0 Radius=1
    g17: Circle CenterX=179.022 CenterY=7.57463 CenterZ=0 NormalX=0 NormalY=0 NormalZ=1 AngleXU=0 Radius=1
    g18: Circle CenterX=179.022 CenterY=5.34704 CenterZ=0 NormalX=0 NormalY=0 NormalZ=1 AngleXU=0 Radius=1
    g19: BSplineCurve PolesCount=3 KnotsCount=2 Degree=2 IsPeriodic=0
    g20: GeomPoint X=175.022 Y=5.37834 Z=0
    g21: GeomPoint X=179.022 Y=5.34704 Z=0
    g22: Circle CenterX=189.124 CenterY=5.37834 CenterZ=0 NormalX=0 NormalY=0 NormalZ=1 AngleXU=0 Radius=1
    g23: Circle CenterX=185.124 CenterY=7.57463 CenterZ=0 NormalX=0 NormalY=0 NormalZ=1 AngleXU=0 Radius=1
    g24: Circle CenterX=185.124 CenterY=5.34704 CenterZ=0 NormalX=0 NormalY=0 NormalZ=1 AngleXU=0 Radius=1
    g25: BSplineCurve PolesCount=3 KnotsCount=2 Degree=2 IsPeriodic=0
    g26: GeomPoint X=189.124 Y=5.37834 Z=0
    g27: GeomPoint X=185.124 Y=5.34704 Z=0
    g28: Circle CenterX=165.871 CenterY=18.1458 CenterZ=0 NormalX=0 NormalY=0 NormalZ=1 AngleXU=0 Radius=1
    g29: Circle CenterX=169.377 CenterY=16.2206 CenterZ=0 NormalX=0 NormalY=0 NormalZ=1 AngleXU=0 Radius=1
    g30: Circle CenterX=165.871 CenterY=14.2954 CenterZ=0 NormalX=0 NormalY=0 NormalZ=1 AngleXU=0 Radius=1
    g31: BSplineCurve PolesCount=3 KnotsCount=2 Degree=2 IsPeriodic=0
    g32: GeomPoint X=165.871 Y=18.1458 Z=0
    g33: GeomPoint X=165.871 Y=14.2954 Z=0
    g34: Circle CenterX=198.275 CenterY=18.1458 CenterZ=0 NormalX=0 NormalY=0 NormalZ=1 AngleXU=0 Radius=1
    g35: Circle CenterX=194.768 CenterY=16.2206 CenterZ=0 NormalX=0 NormalY=0 NormalZ=1 AngleXU=0 Radius=1
    g36: Circle CenterX=198.275 CenterY=14.2954 CenterZ=0 NormalX=0 NormalY=0 NormalZ=1 AngleXU=0 Radius=1
    g37: BSplineCurve PolesCount=3 KnotsCount=2 Degree=2 IsPeriodic=0
    g38: GeomPoint X=198.275 Y=18.1458 Z=0
    g39: GeomPoint X=198.275 Y=14.2954 Z=0
    g40: LineSegment StartX=407.073 StartY=-103.779 StartZ=0 EndX=-42.9272 EndY=-103.779 EndZ=0
    g41: Circle CenterX=125.607 CenterY=54.1951 CenterZ=0 NormalX=0 NormalY=0 NormalZ=1 AngleXU=0 Radius=1
    g42: Circle CenterX=139.632 CenterY=46.4944 CenterZ=0 NormalX=0 NormalY=0 NormalZ=1 AngleXU=0 Radius=1
    g43: Circle CenterX=127.326 CenterY=56.7187 CenterZ=0 NormalX=0 NormalY=0 NormalZ=1 AngleXU=0 Radius=1
    g44: BSplineCurve PolesCount=3 KnotsCount=2 Degree=2 IsPeriodic=0
    g45: GeomPoint X=125.607 Y=54.1951 Z=0
    g46: GeomPoint X=127.326 Y=56.7187 Z=0
    g47: Circle CenterX=236.821 CenterY=56.7187 CenterZ=0 NormalX=0 NormalY=0 NormalZ=1 AngleXU=0 Radius=1
    g48: Circle CenterX=224.513 CenterY=46.4944 CenterZ=0 NormalX=0 NormalY=0 NormalZ=1 AngleXU=0 Radius=1
    g49: Circle CenterX=238.538 CenterY=54.1951 CenterZ=0 NormalX=0 NormalY=0 NormalZ=1 AngleXU=0 Radius=1
    g50: BSplineCurve PolesCount=3 KnotsCount=2 Degree=2 IsPeriodic=0
    g51: GeomPoint X=236.821 Y=56.7187 Z=0
    g52: GeomPoint X=238.538 Y=54.1951 Z=0
    g53: Circle CenterX=238.538 CenterY=-21.7539 CenterZ=0 NormalX=0 NormalY=0 NormalZ=1 AngleXU=0 Radius=1
    g54: Circle CenterX=224.513 CenterY=-14.0532 CenterZ=0 NormalX=0 NormalY=0 NormalZ=1 AngleXU=0 Radius=1
    g55: Circle CenterX=236.821 CenterY=-24.2775 CenterZ=0 NormalX=0 NormalY=0 NormalZ=1 AngleXU=0 Radius=1
    g56: BSplineCurve PolesCount=3 KnotsCount=2 Degree=2 IsPeriodic=0
    g57: GeomPoint X=238.538 Y=-21.7539 Z=0
    g58: GeomPoint X=236.821 Y=-24.2775 Z=0
    g59: Circle CenterX=125.607 CenterY=-21.7539 CenterZ=0 NormalX=0 NormalY=0 NormalZ=1 AngleXU=0 Radius=1
    g60: Circle CenterX=139.632 CenterY=-14.0532 CenterZ=0 NormalX=0 NormalY=0 NormalZ=1 AngleXU=0 Radius=1
    g61: Circle CenterX=127.325 CenterY=-24.2775 CenterZ=0 NormalX=0 NormalY=0 NormalZ=1 AngleXU=0 Radius=1
    g62: BSplineCurve PolesCount=3 KnotsCount=2 Degree=2 IsPeriodic=0
    g63: GeomPoint X=125.607 Y=-21.7539 Z=0
    g64: GeomPoint X=127.325 Y=-24.2775 Z=0
    g65: Circle CenterX=302.996 CenterY=111.695 CenterZ=0 NormalX=0 NormalY=0 NormalZ=1 AngleXU=0 Radius=1
    g66: Circle CenterX=306.073 CenterY=114.251 CenterZ=0 NormalX=0 NormalY=0 NormalZ=1 AngleXU=0 Radius=1
    g67: Circle CenterX=306.073 CenterY=110.251 CenterZ=0 NormalX=0 NormalY=0 NormalZ=1 AngleXU=0 Radius=1
    g68: BSplineCurve PolesCount=3 KnotsCount=2 Degree=2 IsPeriodic=0
    g69: GeomPoint X=302.996 Y=111.695 Z=0
    g70: GeomPoint X=306.073 Y=110.251 Z=0
    g71: Circle CenterX=306.073 CenterY=95.2763 CenterZ=0 NormalX=0 NormalY=0 NormalZ=1 AngleXU=0 Radius=1
    g72: Circle CenterX=306.073 CenterY=91.2763 CenterZ=0 NormalX=0 NormalY=0 NormalZ=1 AngleXU=0 Radius=1
    g73: Circle CenterX=302.567 CenterY=89.3511 CenterZ=0 NormalX=0 NormalY=0 NormalZ=1 AngleXU=0 Radius=1
    g74: BSplineCurve PolesCount=3 KnotsCount=2 Degree=2 IsPeriodic=0
    g75: GeomPoint X=306.073 Y=95.2763 Z=0
    g76: GeomPoint X=302.567 Y=89.3511 Z=0
    g77: LineSegment StartX=306.073 StartY=110.251 StartZ=0 EndX=306.073 EndY=95.2763 EndZ=0
    g78: LineSegment StartX=302.996 StartY=111.695 StartZ=0 EndX=236.821 EndY=56.7187 EndZ=0
    g79: LineSegment StartX=238.538 StartY=54.1951 StartZ=0 EndX=302.567 EndY=89.3511 EndZ=0
    g80: Circle CenterX=61.1496 CenterY=111.695 CenterZ=0 NormalX=0 NormalY=0 NormalZ=1 AngleXU=0 Radius=1
    g81: Circle CenterX=58.0728 CenterY=114.251 CenterZ=0 NormalX=0 NormalY=0 NormalZ=1 AngleXU=0 Radius=1
    g82: Circle CenterX=58.0728 CenterY=110.251 CenterZ=0 NormalX=0 NormalY=0 NormalZ=1 AngleXU=0 Radius=1
    g83: BSplineCurve PolesCount=3 KnotsCount=2 Degree=2 IsPeriodic=0
    g84: GeomPoint X=61.1496 Y=111.695 Z=0
    g85: GeomPoint X=58.0728 Y=110.251 Z=0
    g86: Circle CenterX=61.5791 CenterY=89.3511 CenterZ=0 NormalX=0 NormalY=0 NormalZ=1 AngleXU=0 Radius=1
    g87: Circle CenterX=58.0728 CenterY=91.2763 CenterZ=0 NormalX=0 NormalY=0 NormalZ=1 AngleXU=0 Radius=1
    g88: Circle CenterX=58.0728 CenterY=95.2763 CenterZ=0 NormalX=0 NormalY=0 NormalZ=1 AngleXU=0 Radius=1
    g89: BSplineCurve PolesCount=3 KnotsCount=2 Degree=2 IsPeriodic=0
    g90: GeomPoint X=61.5791 Y=89.3511 Z=0
    g91: GeomPoint X=58.0728 Y=95.2763 Z=0
    g92: LineSegment StartX=58.0728 StartY=110.251 StartZ=0 EndX=58.0728 EndY=95.2763 EndZ=0
    g93: LineSegment StartX=61.1496 StartY=111.695 StartZ=0 EndX=127.326 EndY=56.7187 EndZ=0
    g94: LineSegment StartX=125.607 StartY=54.1951 StartZ=0 EndX=61.5791 EndY=89.3511 EndZ=0
    g95: Circle CenterX=61.5791 CenterY=-56.9099 CenterZ=0 NormalX=0 NormalY=0 NormalZ=1 AngleXU=0 Radius=1
    g96: Circle CenterX=58.0728 CenterY=-58.8351 CenterZ=0 NormalX=0 NormalY=0 NormalZ=1 AngleXU=0 Radius=1
    g97: Circle CenterX=58.0728 CenterY=-62.8351 CenterZ=0 NormalX=0 NormalY=0 NormalZ=1 AngleXU=0 Radius=1
    g98: BSplineCurve PolesCount=3 KnotsCount=2 Degree=2 IsPeriodic=0
    g99: GeomPoint X=61.5791 Y=-56.9099 Z=0
    g100: GeomPoint X=58.0728 Y=-62.8351 Z=0
    g101: Circle CenterX=58.0728 CenterY=-77.8102 CenterZ=0 NormalX=0 NormalY=0 NormalZ=1 AngleXU=0 Radius=1
    g102: Circle CenterX=58.0728 CenterY=-81.8102 CenterZ=0 NormalX=0 NormalY=0 NormalZ=1 AngleXU=0 Radius=1
    g103: Circle CenterX=61.1496 CenterY=-79.2541 CenterZ=0 NormalX=0 NormalY=0 NormalZ=1 AngleXU=0 Radius=1
    g104: BSplineCurve PolesCount=3 KnotsCount=2 Degree=2 IsPeriodic=0
    g105: GeomPoint X=58.0728 Y=-77.8102 Z=0
    g106: GeomPoint X=61.1496 Y=-79.2541 Z=0
    g107: LineSegment StartX=58.0728 StartY=-62.8351 StartZ=0 EndX=58.0728 EndY=-77.8102 EndZ=0
    g108: LineSegment StartX=61.1496 StartY=-79.2541 StartZ=0 EndX=127.325 EndY=-24.2775 EndZ=0
    g109: LineSegment StartX=125.607 StartY=-21.7539 StartZ=0 EndX=61.5791 EndY=-56.9099 EndZ=0
    g110: Circle CenterX=302.567 CenterY=-56.9099 CenterZ=0 NormalX=0 NormalY=0 NormalZ=1 AngleXU=0 Radius=1
    g111: Circle CenterX=306.073 CenterY=-58.8351 CenterZ=0 NormalX=0 NormalY=0 NormalZ=1 AngleXU=0 Radius=1
    g112: Circle CenterX=306.073 CenterY=-62.8351 CenterZ=0 NormalX=0 NormalY=0 NormalZ=1 AngleXU=0 Radius=1
    g113: BSplineCurve PolesCount=3 KnotsCount=2 Degree=2 IsPeriodic=0
    g114: GeomPoint X=302.567 Y=-56.9099 Z=0
    g115: GeomPoint X=306.073 Y=-62.8351 Z=0
    g116: Circle CenterX=302.996 CenterY=-79.2541 CenterZ=0 NormalX=0 NormalY=0 NormalZ=1 AngleXU=0 Radius=1
    g117: Circle CenterX=306.073 CenterY=-81.8102 CenterZ=0 NormalX=0 NormalY=0 NormalZ=1 AngleXU=0 Radius=1
    g118: Circle CenterX=306.073 CenterY=-77.8102 CenterZ=0 NormalX=0 NormalY=0 NormalZ=1 AngleXU=0 Radius=1
    g119: BSplineCurve PolesCount=3 KnotsCount=2 Degree=2 IsPeriodic=0
    g120: GeomPoint X=302.996 Y=-79.2541 Z=0
    g121: GeomPoint X=306.073 Y=-77.8102 Z=0
    g122: LineSegment StartX=306.073 StartY=-62.8351 StartZ=0 EndX=306.073 EndY=-77.8102 EndZ=0
    g123: LineSegment StartX=302.996 StartY=-79.2541 StartZ=0 EndX=236.821 EndY=-24.2775 EndZ=0
    g124: LineSegment StartX=238.538 StartY=-21.7539 StartZ=0 EndX=302.567 EndY=-56.9099 EndZ=0
    g125: Circle CenterX=61.6457 CenterY=-88.8112 CenterZ=0 NormalX=0 NormalY=0 NormalZ=1 AngleXU=0 Radius=1
    g126: Circle CenterX=58.0728 CenterY=-91.7794 CenterZ=0 NormalX=0 NormalY=0 NormalZ=1 AngleXU=0 Radius=1
    g127: Circle CenterX=63.9135 CenterY=-91.7794 CenterZ=0 NormalX=0 NormalY=0 NormalZ=1 AngleXU=0 Radius=1
    g128: BSplineCurve PolesCount=3 KnotsCount=2 Degree=2 IsPeriodic=0
    g129: GeomPoint X=61.6457 Y=-88.8112 Z=0
    g130: GeomPoint X=63.9135 Y=-91.7794 Z=0
    g131: Circle CenterX=179.022 CenterY=-85.8163 CenterZ=0 NormalX=0 NormalY=0 NormalZ=1 AngleXU=0 Radius=1
    g132: Circle CenterX=179.022 CenterY=-91.7794 CenterZ=0 NormalX=0 NormalY=0 NormalZ=1 AngleXU=0 Radius=1
    g133: Circle CenterX=171.895 CenterY=-91.7794 CenterZ=0 NormalX=0 NormalY=0 NormalZ=1 AngleXU=0 Radius=1
    g134: BSplineCurve PolesCount=3 KnotsCount=2 Degree=2 IsPeriodic=0
    g135: GeomPoint X=179.022 Y=-85.8163 Z=0
    g136: GeomPoint X=171.895 Y=-91.7794 Z=0
    g137: Circle CenterX=185.124 CenterY=-86.2028 CenterZ=0 NormalX=0 NormalY=0 NormalZ=1 AngleXU=0 Radius=1
    g138: Circle CenterX=185.124 CenterY=-91.7794 CenterZ=0 NormalX=0 NormalY=0 NormalZ=1 AngleXU=0 Radius=1
    g139: Circle CenterX=191.747 CenterY=-91.7794 CenterZ=0 NormalX=0 NormalY=0 NormalZ=1 AngleXU=0 Radius=1
    g140: BSplineCurve PolesCount=3 KnotsCount=2 Degree=2 IsPeriodic=0
    g141: GeomPoint X=185.124 Y=-86.2028 Z=0
    g142: GeomPoint X=191.747 Y=-91.7794 Z=0
    g143: Circle CenterX=299.888 CenterY=-86.6413 CenterZ=0 NormalX=0 NormalY=0 NormalZ=1 AngleXU=0 Radius=1
    g144: Circle CenterX=306.073 CenterY=-91.7794 CenterZ=0 NormalX=0 NormalY=0 NormalZ=1 AngleXU=0 Radius=1
    g145: Circle CenterX=298.776 CenterY=-91.7794 CenterZ=0 NormalX=0 NormalY=0 NormalZ=1 AngleXU=0 Radius=1
    g146: BSplineCurve PolesCount=3 KnotsCount=2 Degree=2 IsPeriodic=0
    g147: GeomPoint X=299.888 Y=-86.6413 Z=0
    g148: GeomPoint X=298.776 Y=-91.7794 Z=0
    g149: LineSegment StartX=189.124 StartY=5.37834 StartZ=0 EndX=299.888 EndY=-86.6413 EndZ=0
    g150: LineSegment StartX=298.776 StartY=-91.7794 StartZ=0 EndX=191.747 EndY=-91.7794 EndZ=0
    g151: LineSegment StartX=185.124 StartY=-86.2028 StartZ=0 EndX=185.124 EndY=5.34704 EndZ=0
    g152: LineSegment StartX=179.022 StartY=5.34704 StartZ=0 EndX=179.022 EndY=-85.8163 EndZ=0
    g153: LineSegment StartX=171.895 StartY=-91.7794 StartZ=0 EndX=63.9135 EndY=-91.7794 EndZ=0
    g154: LineSegment StartX=61.6457 StartY=-88.8112 StartZ=0 EndX=175.022 EndY=5.37834 EndZ=0
    g155: Circle CenterX=302.073 CenterY=124.221 CenterZ=0 NormalX=0 NormalY=0 NormalZ=1 AngleXU=0 Radius=1
    g156: Circle CenterX=306.073 CenterY=124.221 CenterZ=0 NormalX=0 NormalY=0 NormalZ=1 AngleXU=0 Radius=1
    g157: Circle CenterX=302.996 CenterY=121.665 CenterZ=0 NormalX=0 NormalY=0 NormalZ=1 AngleXU=0 Radius=1
    g158: BSplineCurve PolesCount=3 KnotsCount=2 Degree=2 IsPeriodic=0
    g159: GeomPoint X=302.073 Y=124.221 Z=0
    g160: GeomPoint X=302.996 Y=121.665 Z=0
    g161: Circle CenterX=189.124 CenterY=124.221 CenterZ=0 NormalX=0 NormalY=0 NormalZ=1 AngleXU=0 Radius=1
    g162: Circle CenterX=185.124 CenterY=124.221 CenterZ=0 NormalX=0 NormalY=0 NormalZ=1 AngleXU=0 Radius=1
    g163: Circle CenterX=185.124 CenterY=120.221 CenterZ=0 NormalX=0 NormalY=0 NormalZ=1 AngleXU=0 Radius=1
    g164: BSplineCurve PolesCount=3 KnotsCount=2 Degree=2 IsPeriodic=0
    g165: GeomPoint X=189.124 Y=124.221 Z=0
    g166: GeomPoint X=185.124 Y=120.221 Z=0
    g167: Circle CenterX=175.022 CenterY=124.221 CenterZ=0 NormalX=0 NormalY=0 NormalZ=1 AngleXU=0 Radius=1
    g168: Circle CenterX=179.022 CenterY=124.221 CenterZ=0 NormalX=0 NormalY=0 NormalZ=1 AngleXU=0 Radius=1
    g169: Circle CenterX=179.022 CenterY=120.221 CenterZ=0 NormalX=0 NormalY=0 NormalZ=1 AngleXU=0 Radius=1
    g170: BSplineCurve PolesCount=3 KnotsCount=2 Degree=2 IsPeriodic=0
    g171: GeomPoint X=175.022 Y=124.221 Z=0
    g172: GeomPoint X=179.022 Y=120.221 Z=0
    g173: Circle CenterX=62.0728 CenterY=124.221 CenterZ=0 NormalX=0 NormalY=0 NormalZ=1 AngleXU=0 Radius=1
    g174: Circle CenterX=58.0728 CenterY=124.221 CenterZ=0 NormalX=0 NormalY=0 NormalZ=1 AngleXU=0 Radius=1
    g175: Circle CenterX=61.1496 CenterY=121.665 CenterZ=0 NormalX=0 NormalY=0 NormalZ=1 AngleXU=0 Radius=1
    g176: BSplineCurve PolesCount=3 KnotsCount=2 Degree=2 IsPeriodic=0
    g177: GeomPoint X=62.0728 Y=124.221 Z=0
    g178: GeomPoint X=61.1496 Y=121.665 Z=0
    g179: LineSegment StartX=62.0728 StartY=124.221 StartZ=0 EndX=175.022 EndY=124.221 EndZ=0
    g180: LineSegment StartX=179.022 StartY=120.221 StartZ=0 EndX=179.022 EndY=27.0628 EndZ=0
    g181: LineSegment StartX=185.124 StartY=27.0628 StartZ=0 EndX=185.124 EndY=120.221 EndZ=0
    g182: LineSegment StartX=189.124 StartY=124.221 StartZ=0 EndX=302.073 EndY=124.221 EndZ=0
    g183: LineSegment StartX=302.996 StartY=121.665 StartZ=0 EndX=189.124 EndY=27.0628 EndZ=0
    g184: LineSegment StartX=175.022 StartY=27.0628 StartZ=0 EndX=61.1496 EndY=121.665 EndZ=0
    g185: Circle CenterX=61.5791 CenterY=75.4095 CenterZ=0 NormalX=0 NormalY=0 NormalZ=1 AngleXU=0 Radius=1
    g186: Circle CenterX=58.0728 CenterY=77.3346 CenterZ=0 NormalX=0 NormalY=0 NormalZ=1 AngleXU=0 Radius=1
    g187: Circle CenterX=58.0728 CenterY=73.3346 CenterZ=0 NormalX=0 NormalY=0 NormalZ=1 AngleXU=0 Radius=1
    g188: BSplineCurve PolesCount=3 KnotsCount=2 Degree=2 IsPeriodic=0
    g189: GeomPoint X=61.5791 Y=75.4095 Z=0
    g190: GeomPoint X=58.0728 Y=73.3346 Z=0
    g191: Circle CenterX=58.0728 CenterY=-40.8935 CenterZ=0 NormalX=0 NormalY=0 NormalZ=1 AngleXU=0 Radius=1
    g192: Circle CenterX=58.0728 CenterY=-44.8935 CenterZ=0 NormalX=0 NormalY=0 NormalZ=1 AngleXU=0 Radius=1
    g193: Circle CenterX=61.5791 CenterY=-42.9683 CenterZ=0 NormalX=0 NormalY=0 NormalZ=1 AngleXU=0 Radius=1
    g194: BSplineCurve PolesCount=3 KnotsCount=2 Degree=2 IsPeriodic=0
    g195: GeomPoint X=58.0728 Y=-40.8935 Z=0
    g196: GeomPoint X=61.5791 Y=-42.9683 Z=0
    g197: LineSegment StartX=61.5791 StartY=-42.9683 StartZ=0 EndX=165.871 EndY=14.2954 EndZ=0
    g198: LineSegment StartX=165.871 StartY=18.1458 StartZ=0 EndX=61.5791 EndY=75.4095 EndZ=0
    g199: LineSegment StartX=58.0728 StartY=73.3346 StartZ=0 EndX=58.0728 EndY=-40.8935 EndZ=0
    g200: Circle CenterX=302.567 CenterY=-42.9683 CenterZ=0 NormalX=0 NormalY=0 NormalZ=1 AngleXU=0 Radius=1
    g201: Circle CenterX=306.073 CenterY=-44.8935 CenterZ=0 NormalX=0 NormalY=0 NormalZ=1 AngleXU=0 Radius=1
    g202: Circle CenterX=306.073 CenterY=-40.8935 CenterZ=0 NormalX=0 NormalY=0 NormalZ=1 AngleXU=0 Radius=1
    g203: BSplineCurve PolesCount=3 KnotsCount=2 Degree=2 IsPeriodic=0
    g204: GeomPoint X=302.567 Y=-42.9683 Z=0
    g205: GeomPoint X=306.073 Y=-40.8935 Z=0
    g206: Circle CenterX=306.073 CenterY=73.3346 CenterZ=0 NormalX=0 NormalY=0 NormalZ=1 AngleXU=0 Radius=1
    g207: Circle CenterX=306.073 CenterY=77.3346 CenterZ=0 NormalX=0 NormalY=0 NormalZ=1 AngleXU=0 Radius=1
    g208: Circle CenterX=302.567 CenterY=75.4095 CenterZ=0 NormalX=0 NormalY=0 NormalZ=1 AngleXU=0 Radius=1
    g209: BSplineCurve PolesCount=3 KnotsCount=2 Degree=2 IsPeriodic=0
    g210: GeomPoint X=306.073 Y=73.3346 Z=0
    g211: GeomPoint X=302.567 Y=75.4095 Z=0
    g212: LineSegment StartX=302.567 StartY=-42.9683 StartZ=0 EndX=198.275 EndY=14.2954 EndZ=0
    g213: LineSegment StartX=198.275 StartY=18.1458 StartZ=0 EndX=302.567 EndY=75.4095 EndZ=0
    g214: LineSegment StartX=306.073 StartY=73.3346 StartZ=0 EndX=306.073 EndY=-40.8935 EndZ=0
    g215: LineSegment StartX=322.073 StartY=105.865 StartZ=0 EndX=328.643 EndY=105.865 EndZ=0
    g216: LineSegment StartX=318.073 StartY=120.221 StartZ=0 EndX=318.073 EndY=109.865 EndZ=0
    g217: LineSegment StartX=336.157 StartY=107.779 StartZ=0 EndX=362.567 EndY=122.294 EndZ=0
    g218: Circle CenterX=362.073 CenterY=124.221 CenterZ=0 NormalX=0 NormalY=0 NormalZ=1 AngleXU=0 Radius=1
    g219: Circle CenterX=366.073 CenterY=124.221 CenterZ=0 NormalX=0 NormalY=0 NormalZ=1 AngleXU=0 Radius=1
    g220: Circle CenterX=362.567 CenterY=122.294 CenterZ=0 NormalX=0 NormalY=0 NormalZ=1 AngleXU=0 Radius=1
    g221: BSplineCurve PolesCount=3 KnotsCount=2 Degree=2 IsPeriodic=0
    g222: GeomPoint X=362.073 Y=124.221 Z=0
    g223: GeomPoint X=362.567 Y=122.294 Z=0
    g224: Circle CenterX=322.073 CenterY=124.221 CenterZ=0 NormalX=0 NormalY=0 NormalZ=1 AngleXU=0 Radius=1
    g225: Circle CenterX=318.073 CenterY=124.221 CenterZ=0 NormalX=0 NormalY=0 NormalZ=1 AngleXU=0 Radius=1
    g226: Circle CenterX=318.073 CenterY=120.221 CenterZ=0 NormalX=0 NormalY=0 NormalZ=1 AngleXU=0 Radius=1
    g227: BSplineCurve PolesCount=3 KnotsCount=2 Degree=2 IsPeriodic=0
    g228: GeomPoint X=322.073 Y=124.221 Z=0
    g229: GeomPoint X=318.073 Y=120.221 Z=0
    g230: Circle CenterX=322.073 CenterY=105.865 CenterZ=0 NormalX=0 NormalY=0 NormalZ=1 AngleXU=0 Radius=1
    g231: Circle CenterX=318.073 CenterY=105.865 CenterZ=0 NormalX=0 NormalY=0 NormalZ=1 AngleXU=0 Radius=1
    g232: Circle CenterX=318.073 CenterY=109.865 CenterZ=0 NormalX=0 NormalY=0 NormalZ=1 AngleXU=0 Radius=1
    g233: BSplineCurve PolesCount=3 KnotsCount=2 Degree=2 IsPeriodic=0
    g234: GeomPoint X=322.073 Y=105.865 Z=0
    g235: GeomPoint X=318.073 Y=109.865 Z=0
    g236: Circle CenterX=336.157 CenterY=107.779 CenterZ=0 NormalX=0 NormalY=0 NormalZ=1 AngleXU=0 Radius=1
    g237: Circle CenterX=332.651 CenterY=105.853 CenterZ=0 NormalX=0 NormalY=0 NormalZ=1 AngleXU=0 Radius=1
    g238: Circle CenterX=328.643 CenterY=105.865 CenterZ=0 NormalX=0 NormalY=0 NormalZ=1 AngleXU=0 Radius=1
    g239: BSplineCurve PolesCount=3 KnotsCount=2 Degree=2 IsPeriodic=0
    g240: GeomPoint X=336.157 Y=107.779 Z=0
    g241: GeomPoint X=328.643 Y=105.865 Z=0
    g242: LineSegment StartX=322.073 StartY=124.221 StartZ=0 EndX=362.073 EndY=124.221 EndZ=0
    g243: Circle CenterX=371.567 CenterY=-80.8644 CenterZ=0 NormalX=0 NormalY=0 NormalZ=1 AngleXU=0 Radius=1
    g244: Circle CenterX=375.073 CenterY=-82.7896 CenterZ=0 NormalX=0 NormalY=0 NormalZ=1 AngleXU=0 Radius=1
    g245: Circle CenterX=375.073 CenterY=-78.7896 CenterZ=0 NormalX=0 NormalY=0 NormalZ=1 AngleXU=0 Radius=1
    g246: BSplineCurve PolesCount=3 KnotsCount=2 Degree=2 IsPeriodic=0
    g247: GeomPoint X=371.567 Y=-80.8644 Z=0
    g248: GeomPoint X=375.073 Y=-78.7896 Z=0
    g249: Circle CenterX=321.579 CenterY=-53.4075 CenterZ=0 NormalX=0 NormalY=0 NormalZ=1 AngleXU=0 Radius=1
    g250: Circle CenterX=318.073 CenterY=-51.4823 CenterZ=0 NormalX=0 NormalY=0 NormalZ=1 AngleXU=0 Radius=1
    g251: Circle CenterX=318.073 CenterY=-47.4805 CenterZ=0 NormalX=0 NormalY=0 NormalZ=1 AngleXU=0 Radius=1
    g252: BSplineCurve PolesCount=3 KnotsCount=2 Degree=2 IsPeriodic=0
    g253: GeomPoint X=321.579 Y=-53.4075 Z=0
    g254: GeomPoint X=318.073 Y=-47.4805 Z=0
    g255: LineSegment StartX=371.567 StartY=-80.8644 StartZ=0 EndX=321.579 EndY=-53.4075 EndZ=0
    g256: Circle CenterX=321.579 CenterY=-67.3492 CenterZ=0 NormalX=0 NormalY=0 NormalZ=1 AngleXU=0 Radius=1
    g257: Circle CenterX=318.073 CenterY=-65.424 CenterZ=0 NormalX=0 NormalY=0 NormalZ=1 AngleXU=0 Radius=1
    g258: Circle CenterX=318.073 CenterY=-69.424 CenterZ=0 NormalX=0 NormalY=0 NormalZ=1 AngleXU=0 Radius=1
    g259: BSplineCurve PolesCount=3 KnotsCount=2 Degree=2 IsPeriodic=0
    g260: GeomPoint X=321.579 Y=-67.3492 Z=0
    g261: GeomPoint X=318.073 Y=-69.424 Z=0
    g262: Circle CenterX=362.567 CenterY=-89.8542 CenterZ=0 NormalX=0 NormalY=0 NormalZ=1 AngleXU=0 Radius=1
    g263: Circle CenterX=366.073 CenterY=-91.7794 CenterZ=0 NormalX=0 NormalY=0 NormalZ=1 AngleXU=0 Radius=1
    g264: Circle CenterX=362.073 CenterY=-91.7794 CenterZ=0 NormalX=0 NormalY=0 NormalZ=1 AngleXU=0 Radius=1
    g265: BSplineCurve PolesCount=3 KnotsCount=2 Degree=2 IsPeriodic=0
    g266: GeomPoint X=362.567 Y=-89.8542 Z=0
    g267: GeomPoint X=362.073 Y=-91.7794 Z=0
    g268: Circle CenterX=322.073 CenterY=-91.7794 CenterZ=0 NormalX=0 NormalY=0 NormalZ=1 AngleXU=0 Radius=1
    g269: Circle CenterX=318.073 CenterY=-91.7794 CenterZ=0 NormalX=0 NormalY=0 NormalZ=1 AngleXU=0 Radius=1
    g270: Circle CenterX=318.073 CenterY=-87.7794 CenterZ=0 NormalX=0 NormalY=0 NormalZ=1 AngleXU=0 Radius=1
    g271: BSplineCurve PolesCount=3 KnotsCount=2 Degree=2 IsPeriodic=0
    g272: GeomPoint X=322.073 Y=-91.7794 Z=0
    g273: GeomPoint X=318.073 Y=-87.7794 Z=0
    g274: LineSegment StartX=362.567 StartY=-89.8542 StartZ=0 EndX=321.579 EndY=-67.3492 EndZ=0
    g275: LineSegment StartX=318.073 StartY=-69.424 StartZ=0 EndX=318.073 EndY=-87.7794 EndZ=0
    g276: LineSegment StartX=322.073 StartY=-91.7794 StartZ=0 EndX=362.073 EndY=-91.7794 EndZ=0
    g277: Circle CenterX=2.07281 CenterY=124.221 CenterZ=0 NormalX=0 NormalY=0 NormalZ=1 AngleXU=0 Radius=1
    g278: Circle CenterX=1.57905 CenterY=122.295 CenterZ=0 NormalX=0 NormalY=0 NormalZ=1 AngleXU=0 Radius=1
    g279: BSplineCurve PolesCount=3 KnotsCount=2 Degree=2 IsPeriodic=0
    g280: GeomPoint X=2.07281 Y=124.221 Z=0
    g281: GeomPoint X=1.57905 Y=122.295 Z=0
    g282: Circle CenterX=42.0728 CenterY=124.221 CenterZ=0 NormalX=0 NormalY=0 NormalZ=1 AngleXU=0 Radius=1
    g283: Circle CenterX=46.0728 CenterY=124.221 CenterZ=0 NormalX=0 NormalY=0 NormalZ=1 AngleXU=0 Radius=1
    g284: Circle CenterX=46.0728 CenterY=120.221 CenterZ=0 NormalX=0 NormalY=0 NormalZ=1 AngleXU=0 Radius=1
    g285: BSplineCurve PolesCount=3 KnotsCount=2 Degree=2 IsPeriodic=0
    g286: GeomPoint X=42.0728 Y=124.221 Z=0
    g287: GeomPoint X=46.0728 Y=120.221 Z=0
    g288: Circle CenterX=46.0728 CenterY=109.865 CenterZ=0 NormalX=0 NormalY=0 NormalZ=1 AngleXU=0 Radius=1
    g289: Circle CenterX=46.0728 CenterY=105.865 CenterZ=0 NormalX=0 NormalY=0 NormalZ=1 AngleXU=0 Radius=1
    g290: Circle CenterX=42.0728 CenterY=105.865 CenterZ=0 NormalX=0 NormalY=0 NormalZ=1 AngleXU=0 Radius=1
    g291: BSplineCurve PolesCount=3 KnotsCount=2 Degree=2 IsPeriodic=0
    g292: GeomPoint X=46.0728 Y=109.865 Z=0
    g293: GeomPoint X=42.0728 Y=105.865 Z=0
    g294: Circle CenterX=35.5028 CenterY=105.865 CenterZ=0 NormalX=0 NormalY=0 NormalZ=1 AngleXU=0 Radius=1
    g295: Circle CenterX=31.5028 CenterY=105.865 CenterZ=0 NormalX=0 NormalY=0 NormalZ=1 AngleXU=0 Radius=1
    g296: Circle CenterX=27.9965 CenterY=107.79 CenterZ=0 NormalX=0 NormalY=0 NormalZ=1 AngleXU=0 Radius=1
    g297: BSplineCurve PolesCount=3 KnotsCount=2 Degree=2 IsPeriodic=0
    g298: GeomPoint X=35.5028 Y=105.865 Z=0
    g299: GeomPoint X=27.9965 Y=107.79 Z=0
    g300: LineSegment StartX=2.07281 StartY=124.221 StartZ=0 EndX=42.0728 EndY=124.221 EndZ=0
    g301: LineSegment StartX=46.0728 StartY=120.221 StartZ=0 EndX=46.0728 EndY=109.865 EndZ=0
    g302: LineSegment StartX=42.0728 StartY=105.865 StartZ=0 EndX=35.5028 EndY=105.865 EndZ=0
    g303: LineSegment StartX=27.9965 StartY=107.79 StartZ=0 EndX=1.57905 EndY=122.295 EndZ=0
    g304: Circle CenterX=42.5666 CenterY=-67.3492 CenterZ=0 NormalX=0 NormalY=0 NormalZ=1 AngleXU=0 Radius=1
    g305: Circle CenterX=46.0728 CenterY=-65.424 CenterZ=0 NormalX=0 NormalY=0 NormalZ=1 AngleXU=0 Radius=1
    g306: Circle CenterX=46.0728 CenterY=-69.424 CenterZ=0 NormalX=0 NormalY=0 NormalZ=1 AngleXU=0 Radius=1
    g307: BSplineCurve PolesCount=3 KnotsCount=2 Degree=2 IsPeriodic=0
    g308: GeomPoint X=42.5666 Y=-67.3492 Z=0
    g309: GeomPoint X=46.0728 Y=-69.424 Z=0
    g310: Circle CenterX=46.0728 CenterY=-87.7794 CenterZ=0 NormalX=0 NormalY=0 NormalZ=1 AngleXU=0 Radius=1
    g311: Circle CenterX=46.0728 CenterY=-91.7794 CenterZ=0 NormalX=0 NormalY=0 NormalZ=1 AngleXU=0 Radius=1
    g312: Circle CenterX=42.0728 CenterY=-91.7794 CenterZ=0 NormalX=0 NormalY=0 NormalZ=1 AngleXU=0 Radius=1
    g313: BSplineCurve PolesCount=3 KnotsCount=2 Degree=2 IsPeriodic=0
    g314: GeomPoint X=46.0728 Y=-87.7794 Z=0
    g315: GeomPoint X=42.0728 Y=-91.7794 Z=0
    g316: Circle CenterX=2.07281 CenterY=-91.7794 CenterZ=0 NormalX=0 NormalY=0 NormalZ=1 AngleXU=0 Radius=1
    g317: Circle CenterX=-1.92719 CenterY=-91.7794 CenterZ=0 NormalX=0 NormalY=0 NormalZ=1 AngleXU=0 Radius=1
    g318: Circle CenterX=1.57905 CenterY=-89.8542 CenterZ=0 NormalX=0 NormalY=0 NormalZ=1 AngleXU=0 Radius=1
    g319: BSplineCurve PolesCount=3 KnotsCount=2 Degree=2 IsPeriodic=0
    g320: GeomPoint X=2.07281 Y=-91.7794 Z=0
    g321: GeomPoint X=1.57905 Y=-89.8542 Z=0
    g322: LineSegment StartX=2.07281 StartY=-91.7794 StartZ=0 EndX=42.0728 EndY=-91.7794 EndZ=0
    g323: LineSegment StartX=46.0728 StartY=-87.7794 StartZ=0 EndX=46.0728 EndY=-69.424 EndZ=0
    g324: LineSegment StartX=42.5666 StartY=-67.3492 StartZ=0 EndX=1.57905 EndY=-89.8542 EndZ=0
    g325: Circle CenterX=322.073 CenterY=76.4095 CenterZ=0 NormalX=0 NormalY=0 NormalZ=1 AngleXU=0 Radius=4
    g326: BSplineCurve PolesCount=3 KnotsCount=2 Degree=2 IsPeriodic=0
    g327: GeomPoint X=318.073 Y=72.4095 Z=0
    g328: GeomPoint X=322.073 Y=76.4095 Z=0
    g329: Circle CenterX=375.073 CenterY=72.4095 CenterZ=0 NormalX=0 NormalY=0 NormalZ=1 AngleXU=0 Radius=1
    g330: Circle CenterX=375.073 CenterY=76.4095 CenterZ=0 NormalX=0 NormalY=0 NormalZ=1 AngleXU=0 Radius=1
    g331: Circle CenterX=371.073 CenterY=76.4095 CenterZ=0 NormalX=0 NormalY=0 NormalZ=1 AngleXU=0 Radius=1
    g332: BSplineCurve PolesCount=3 KnotsCount=2 Degree=2 IsPeriodic=0
    g333: GeomPoint X=375.073 Y=72.4095 Z=0
    g334: GeomPoint X=371.073 Y=76.4095 Z=0
    g335: LineSegment StartX=322.073 StartY=76.4095 StartZ=0 EndX=371.073 EndY=76.4095 EndZ=0
    g336: LineSegment StartX=318.073 StartY=72.4095 StartZ=0 EndX=318.073 EndY=-47.4805 EndZ=0
    g337: LineSegment StartX=375.073 StartY=72.4095 StartZ=0 EndX=375.073 EndY=-78.7896 EndZ=0
    g338: ArcOfCircle CenterX=-26.9272 CenterY=22.1087 CenterZ=0 NormalX=0 NormalY=0 NormalZ=1 AngleXU=0 Radius=4 StartAngle=5e-16 EndAngle=3.14159
    g339: LineSegment StartX=-22.9272 StartY=22.1087 StartZ=0 EndX=-18.9272 EndY=-83.7794 EndZ=0
    g340: LineSegment StartX=-34.9272 StartY=-83.7794 StartZ=0 EndX=-30.9272 EndY=22.1087 EndZ=0
    g341: ArcOfCircle CenterX=391.073 CenterY=22.1087 CenterZ=0 NormalX=0 NormalY=0 NormalZ=1 AngleXU=0 Radius=4 StartAngle=0 EndAngle=3.14159
    g342: LineSegment StartX=387.073 StartY=22.1087 StartZ=0 EndX=383.073 EndY=-83.7794 EndZ=0
    g343: LineSegment StartX=395.073 StartY=22.1087 StartZ=0 EndX=399.073 EndY=-83.7794 EndZ=0
    g344: Circle CenterX=-10.9272 CenterY=-78.7794 CenterZ=0 NormalX=0 NormalY=0 NormalZ=1 AngleXU=0 Radius=1
    g345: Circle CenterX=-10.9272 CenterY=-82.7794 CenterZ=0 NormalX=0 NormalY=0 NormalZ=1 AngleXU=0 Radius=1
    g346: Circle CenterX=-7.42095 CenterY=-80.8542 CenterZ=0 NormalX=0 NormalY=0 NormalZ=1 AngleXU=0 Radius=1
    g347: BSplineCurve PolesCount=3 KnotsCount=2 Degree=2 IsPeriodic=0
    g348: GeomPoint X=-10.9272 Y=-78.7794 Z=0
    g349: GeomPoint X=-7.42095 Y=-80.8542 Z=0
    g350: Circle CenterX=42.5666 CenterY=-53.4075 CenterZ=0 NormalX=0 NormalY=0 NormalZ=1 AngleXU=0 Radius=1
    g351: Circle CenterX=46.0728 CenterY=-51.4823 CenterZ=0 NormalX=0 NormalY=0 NormalZ=1 AngleXU=0 Radius=1
    g352: Circle CenterX=46.0728 CenterY=-47.4823 CenterZ=0 NormalX=0 NormalY=0 NormalZ=1 AngleXU=0 Radius=1
    g353: BSplineCurve PolesCount=3 KnotsCount=2 Degree=2 IsPeriodic=0
    g354: GeomPoint X=42.5666 Y=-53.4075 Z=0
    g355: GeomPoint X=46.0728 Y=-47.4823 Z=0
    g356: Circle CenterX=46.0728 CenterY=72.4095 CenterZ=0 NormalX=0 NormalY=0 NormalZ=1 AngleXU=0 Radius=1
    g357: Circle CenterX=46.0728 CenterY=76.4095 CenterZ=0 NormalX=0 NormalY=0 NormalZ=1 AngleXU=0 Radius=1
    g358: Circle CenterX=42.0728 CenterY=76.4095 CenterZ=0 NormalX=0 NormalY=0 NormalZ=1 AngleXU=0 Radius=1
    g359: BSplineCurve PolesCount=3 KnotsCount=2 Degree=2 IsPeriodic=0
    g360: GeomPoint X=46.0728 Y=72.4095 Z=0
    g361: GeomPoint X=42.0728 Y=76.4095 Z=0
    g362: Circle CenterX=-6.92718 CenterY=76.4095 CenterZ=0 NormalX=0 NormalY=0 NormalZ=1 AngleXU=0 Radius=1
    g363: Circle CenterX=-10.9272 CenterY=76.4095 CenterZ=0 NormalX=0 NormalY=0 NormalZ=1 AngleXU=0 Radius=1
    g364: Circle CenterX=-10.9272 CenterY=72.4095 CenterZ=0 NormalX=0 NormalY=0 NormalZ=1 AngleXU=0 Radius=1
    g365: BSplineCurve PolesCount=3 KnotsCount=2 Degree=2 IsPeriodic=0
    g366: GeomPoint X=-6.92718 Y=76.4095 Z=0
    g367: GeomPoint X=-10.9272 Y=72.4095 Z=0
    g368: LineSegment StartX=-10.9272 StartY=72.4095 StartZ=0 EndX=-10.9272 EndY=-78.7794 EndZ=0
    g369: LineSegment StartX=-7.42095 StartY=-80.8542 StartZ=0 EndX=42.5666 EndY=-53.4075 EndZ=0
    g370: LineSegment StartX=46.0728 StartY=-47.4823 StartZ=0 EndX=46.0728 EndY=72.4095 EndZ=0
    g371: LineSegment StartX=42.0728 StartY=76.4095 StartZ=0 EndX=-6.92719 EndY=76.4095 EndZ=0
    g372: LineSegment StartX=182.072 StartY=136.221 StartZ=0 EndX=182.072 EndY=137.404 EndZ=0
    g373: LineSegment StartX=182.072 StartY=136.221 StartZ=0 EndX=232.072 EndY=136.221 EndZ=0
    g374: LineSegment StartX=182.072 StartY=136.221 StartZ=0 EndX=132.072 EndY=136.221 EndZ=0
    g375: LineSegment StartX=232.072 StartY=136.221 StartZ=0 EndX=232.072 EndY=-117.815 EndZ=0
    g376: LineSegment StartX=132.072 StartY=136.221 StartZ=0 EndX=132.072 EndY=-121.309 EndZ=0
    g377: LineSegment StartX=132.072 StartY=136.221 StartZ=0 EndX=120.075 EndY=136.221 EndZ=0
  constraints (624):
    c: Vertical(g0)
    c: Vertical(g1)
    c: Block(g1)
    c: Block(g0)
    c: Weight(g4) = 1
    c: Equal(g4,g5)
    c: Equal(g4,g6)
    c: InternalAlignment(g4,g7)
    c: InternalAlignment(g5,g7)
    c: InternalAlignment(g6,g7)
    c: InternalAlignment(g8,g7)
    c: InternalAlignment(g9,g7)
    c: Weight(g10) = 1
    c: Equal(g10,g11)
    c: Equal(g10,g12)
    c: InternalAlignment(g10,g13)
    c: InternalAlignment(g11,g13)
    c: InternalAlignment(g12,g13)
    c: InternalAlignment(g14,g13)
    c: InternalAlignment(g15,g13)
    c: Block(g13)
    c: Block(g7)
    c: Weight(g16) = 1
    c: Equal(g16,g17)
    c: Equal(g16,g18)
    c: InternalAlignment(g16,g19)
    c: InternalAlignment(g17,g19)
    c: InternalAlignment(g18,g19)
    c: InternalAlignment(g20,g19)
    c: InternalAlignment(g21,g19)
    c: Weight(g22) = 1
    c: Equal(g22,g23)
    c: Equal(g22,g24)
    c: InternalAlignment(g22,g25)
    c: InternalAlignment(g23,g25)
    c: InternalAlignment(g24,g25)
    c: InternalAlignment(g26,g25)
    c: InternalAlignment(g27,g25)
    c: Block(g25)
    c: Block(g19)
    c: Weight(g28) = 1
    c: Equal(g28,g29)
    c: Equal(g28,g30)
    c: InternalAlignment(g28,g31)
    c: InternalAlignment(g29,g31)
    c: InternalAlignment(g30,g31)
    c: InternalAlignment(g32,g31)
    c: InternalAlignment(g33,g31)
    c: Weight(g34) = 1
    c: Equal(g34,g35)
    c: Equal(g34,g36)
    c: InternalAlignment(g34,g37)
    c: InternalAlignment(g35,g37)
    c: InternalAlignment(g36,g37)
    c: InternalAlignment(g38,g37)
    c: InternalAlignment(g39,g37)
    c: Block(g31)
    c: Block(g37)
    c: Coincident(g40,g1)
    c: Coincident(g40,g0)
    c: Horizontal(g40)
    c: Distance(g40) = 450
    c: Weight(g41) = 1
    c: Equal(g41,g42)
    c: Equal(g41,g43)
    c: InternalAlignment(g41,g44)
    c: InternalAlignment(g42,g44)
    c: InternalAlignment(g43,g44)
    c: InternalAlignment(g45,g44)
    c: InternalAlignment(g46,g44)
    c: Block(g44)
    c: Weight(g47) = 1
    c: Equal(g47,g48)
    c: Equal(g47,g49)
    c: InternalAlignment(g47,g50)
    c: InternalAlignment(g48,g50)
    c: InternalAlignment(g49,g50)
    c: InternalAlignment(g51,g50)
    c: InternalAlignment(g52,g50)
    c: Block(g50)
    c: Weight(g53) = 1
    c: Equal(g53,g54)
    c: Equal(g53,g55)
    c: InternalAlignment(g53,g56)
    c: InternalAlignment(g54,g56)
    c: InternalAlignment(g55,g56)
    c: InternalAlignment(g57,g56)
    c: InternalAlignment(g58,g56)
    c: Block(g56)
    c: Weight(g59) = 1
    c: Equal(g59,g60)
    c: Equal(g59,g61)
    c: InternalAlignment(g59,g62)
    c: InternalAlignment(g60,g62)
    c: InternalAlignment(g61,g62)
    c: InternalAlignment(g63,g62)
    c: InternalAlignment(g64,g62)
    c: Block(g62)
    c: Weight(g65) = 1
    c: Equal(g65,g66)
    c: Equal(g65,g67)
    c: InternalAlignment(g65,g68)
    c: InternalAlignment(g66,g68)
    c: InternalAlignment(g67,g68)
    c: InternalAlignment(g69,g68)
    c: InternalAlignment(g70,g68)
    c: Weight(g71) = 1
    c: Equal(g71,g72)
    c: Equal(g71,g73)
    c: InternalAlignment(g71,g74)
    c: InternalAlignment(g72,g74)
    c: InternalAlignment(g73,g74)
    c: InternalAlignment(g75,g74)
    c: InternalAlignment(g76,g74)
    c: Block(g68)
    c: Block(g74)
    c: Coincident(g77,g68)
    c: Coincident(g77,g74)
    c: Vertical(g77)
    c: Coincident(g78,g68)
    c: Coincident(g78,g50)
    c: Coincident(g79,g50)
    c: Coincident(g79,g74)
    c: Weight(g80) = 1
    c: Equal(g80,g81)
    c: Equal(g80,g82)
    c: InternalAlignment(g80,g83)
    c: InternalAlignment(g81,g83)
    c: InternalAlignment(g82,g83)
    c: InternalAlignment(g84,g83)
    c: InternalAlignment(g85,g83)
    c: Weight(g86) = 1
    c: Equal(g86,g87)
    c: Equal(g86,g88)
    c: InternalAlignment(g86,g89)
    c: InternalAlignment(g87,g89)
    c: InternalAlignment(g88,g89)
    c: InternalAlignment(g90,g89)
    c: InternalAlignment(g91,g89)
    c: Block(g83)
    c: Block(g89)
    c: Coincident(g92,g83)
    c: Coincident(g92,g89)
    c: Vertical(g92)
    c: Coincident(g93,g83)
    c: Coincident(g93,g44)
    c: Coincident(g94,g44)
    c: Coincident(g94,g89)
    c: Weight(g95) = 1
    c: Equal(g95,g96)
    c: Equal(g95,g97)
    c: InternalAlignment(g95,g98)
    c: InternalAlignment(g96,g98)
    c: InternalAlignment(g97,g98)
    c: InternalAlignment(g99,g98)
    c: InternalAlignment(g100,g98)
    c: Weight(g101) = 1
    c: Equal(g101,g102)
    c: Equal(g101,g103)
    c: InternalAlignment(g101,g104)
    c: InternalAlignment(g102,g104)
    c: InternalAlignment(g103,g104)
    c: InternalAlignment(g105,g104)
    c: InternalAlignment(g106,g104)
    c: Block(g98)
    c: Block(g104)
    c: Coincident(g107,g98)
    c: Coincident(g107,g104)
    c: Vertical(g107)
    c: Coincident(g108,g104)
    c: Coincident(g108,g62)
    c: Coincident(g109,g62)
    c: Coincident(g109,g98)
    c: Weight(g110) = 1
    c: Equal(g110,g111)
    c: Equal(g110,g112)
    c: InternalAlignment(g110,g113)
    c: InternalAlignment(g111,g113)
    c: InternalAlignment(g112,g113)
    c: InternalAlignment(g114,g113)
    c: InternalAlignment(g115,g113)
    c: Weight(g116) = 1
    c: Equal(g116,g117)
    c: Equal(g116,g118)
    c: InternalAlignment(g116,g119)
    c: InternalAlignment(g117,g119)
    c: InternalAlignment(g118,g119)
    c: InternalAlignment(g120,g119)
    c: InternalAlignment(g121,g119)
    c: Block(g113)
    c: Block(g119)
    c: Coincident(g122,g113)
    c: Coincident(g122,g119)
    c: Vertical(g122)
    c: Coincident(g123,g119)
    c: Coincident(g123,g56)
    c: Coincident(g124,g56)
    c: Coincident(g124,g113)
    c: Weight(g125) = 1
    c: Equal(g125,g126)
    c: Equal(g125,g127)
    c: InternalAlignment(g125,g128)
    c: InternalAlignment(g126,g128)
    c: InternalAlignment(g127,g128)
    c: InternalAlignment(g129,g128)
    c: InternalAlignment(g130,g128)
    c: Weight(g131) = 1
    c: Equal(g131,g132)
    c: Equal(g131,g133)
    c: InternalAlignment(g131,g134)
    c: InternalAlignment(g132,g134)
    c: InternalAlignment(g133,g134)
    c: InternalAlignment(g135,g134)
    c: InternalAlignment(g136,g134)
    c: Weight(g137) = 1
    c: Equal(g137,g138)
    c: Equal(g137,g139)
    c: InternalAlignment(g137,g140)
    c: InternalAlignment(g138,g140)
    c: InternalAlignment(g139,g140)
    c: InternalAlignment(g141,g140)
    c: InternalAlignment(g142,g140)
    c: Weight(g143) = 1
    c: Equal(g143,g144)
    c: Equal(g143,g145)
    c: InternalAlignment(g143,g146)
    c: InternalAlignment(g144,g146)
    c: InternalAlignment(g145,g146)
    c: InternalAlignment(g147,g146)
    c: InternalAlignment(g148,g146)
    c: Block(g146)
    c: Block(g140)
    c: Block(g134)
    c: Block(g128)
    c: Coincident(g149,g25)
    c: Coincident(g149,g146)
    c: Coincident(g150,g146)
    c: Coincident(g150,g140)
    c: Horizontal(g150)
    c: Coincident(g151,g140)
    c: Coincident(g151,g25)
    c: Vertical(g151)
    c: Coincident(g152,g19)
    c: Coincident(g152,g134)
    c: Vertical(g152)
    c: Coincident(g153,g134)
    c: Coincident(g153,g128)
    c: Horizontal(g153)
    c: Coincident(g154,g128)
    c: Coincident(g154,g19)
    c: Weight(g155) = 1
    c: Equal(g155,g156)
    c: Equal(g155,g157)
    c: InternalAlignment(g155,g158)
    c: InternalAlignment(g156,g158)
    c: InternalAlignment(g157,g158)
    c: InternalAlignment(g159,g158)
    c: InternalAlignment(g160,g158)
    c: Weight(g161) = 1
    c: Equal(g161,g162)
    c: Equal(g161,g163)
    c: InternalAlignment(g161,g164)
    c: InternalAlignment(g162,g164)
    c: InternalAlignment(g163,g164)
    c: InternalAlignment(g165,g164)
    c: InternalAlignment(g166,g164)
    c: Weight(g167) = 1
    c: Equal(g167,g168)
    c: Equal(g167,g169)
    c: InternalAlignment(g167,g170)
    c: InternalAlignment(g168,g170)
    c: InternalAlignment(g169,g170)
    c: InternalAlignment(g171,g170)
    c: InternalAlignment(g172,g170)
    c: Weight(g173) = 1
    c: Equal(g173,g174)
    c: Equal(g173,g175)
    c: InternalAlignment(g173,g176)
    c: InternalAlignment(g174,g176)
    c: InternalAlignment(g175,g176)
    c: InternalAlignment(g177,g176)
    c: InternalAlignment(g178,g176)
    c: Block(g176)
    c: Block(g170)
    c: Block(g164)
    c: Block(g158)
    c: Coincident(g179,g176)
    c: Coincident(g179,g170)
    c: Horizontal(g179)
    c: Coincident(g180,g170)
    c: Coincident(g180,g7)
    c: Vertical(g180)
    c: Coincident(g181,g13)
    c: Coincident(g181,g164)
    c: Vertical(g181)
    c: Coincident(g182,g164)
    c: Coincident(g182,g158)
    c: Horizontal(g182)
    c: Coincident(g183,g158)
    c: Coincident(g183,g13)
    c: Coincident(g184,g7)
    c: Weight(g185) = 1
    c: Equal(g185,g186)
    c: Equal(g185,g187)
    c: InternalAlignment(g185,g188)
    c: InternalAlignment(g186,g188)
    c: InternalAlignment(g187,g188)
    c: InternalAlignment(g189,g188)
    c: InternalAlignment(g190,g188)
    c: Weight(g191) = 1
    c: Equal(g191,g192)
    c: Equal(g191,g193)
    c: InternalAlignment(g191,g194)
    c: InternalAlignment(g192,g194)
    c: InternalAlignment(g193,g194)
    c: InternalAlignment(g195,g194)
    c: InternalAlignment(g196,g194)
    c: Block(g194)
    c: Block(g188)
    c: Coincident(g197,g194)
    c: Coincident(g197,g31)
    c: Coincident(g198,g31)
    c: Coincident(g198,g188)
    c: Coincident(g199,g188)
    c: Coincident(g199,g194)
    c: Vertical(g199)
    c: Weight(g200) = 1
    c: Equal(g200,g201)
    c: Equal(g200,g202)
    c: InternalAlignment(g200,g203)
    c: InternalAlignment(g201,g203)
    c: InternalAlignment(g202,g203)
    c: InternalAlignment(g204,g203)
    c: InternalAlignment(g205,g203)
    c: Weight(g206) = 1
    c: Equal(g206,g207)
    c: Equal(g206,g208)
    c: InternalAlignment(g206,g209)
    c: InternalAlignment(g207,g209)
    c: InternalAlignment(g208,g209)
    c: InternalAlignment(g210,g209)
    c: InternalAlignment(g211,g209)
    c: Block(g209)
    c: Block(g203)
    c: Coincident(g212,g203)
    c: Coincident(g212,g37)
    c: Coincident(g213,g37)
    c: Coincident(g213,g209)
    c: Coincident(g214,g209)
    c: Coincident(g214,g203)
    c: Vertical(g214)
    c: Horizontal(g215)
    c: Block(g215)
    c: Vertical(g216)
    c: Block(g216)
    c: Block(g217)
    c: Weight(g218) = 1
    c: Equal(g218,g219)
    c: Equal(g218,g220)
    c: InternalAlignment(g218,g221)
    c: InternalAlignment(g219,g221)
    c: InternalAlignment(g220,g221)
    c: InternalAlignment(g222,g221)
    c: InternalAlignment(g223,g221)
    c: Weight(g224) = 1
    c: Equal(g224,g225)
    c: Equal(g224,g226)
    c: InternalAlignment(g224,g227)
    c: InternalAlignment(g225,g227)
    c: InternalAlignment(g226,g227)
    c: InternalAlignment(g228,g227)
    c: InternalAlignment(g229,g227)
    c: Weight(g230) = 1
    c: Equal(g230,g231)
    c: Equal(g230,g232)
    c: InternalAlignment(g230,g233)
    c: InternalAlignment(g231,g233)
    c: InternalAlignment(g232,g233)
    c: InternalAlignment(g234,g233)
    c: InternalAlignment(g235,g233)
    c: Weight(g236) = 1
    c: Equal(g236,g237)
    c: Equal(g236,g238)
    c: InternalAlignment(g236,g239)
    c: InternalAlignment(g237,g239)
    c: InternalAlignment(g238,g239)
    c: InternalAlignment(g240,g239)
    c: InternalAlignment(g241,g239)
    c: Block(g221)
    c: Block(g227)
    c: Block(g233)
    c: Block(g239)
    c: Coincident(g242,g227)
    c: Coincident(g242,g221)
    c: Horizontal(g242)
    c: Block(g184)
    c: Weight(g243) = 1
    c: Equal(g243,g244)
    c: Equal(g243,g245)
    c: InternalAlignment(g243,g246)
    c: InternalAlignment(g244,g246)
    c: InternalAlignment(g245,g246)
    c: InternalAlignment(g247,g246)
    c: InternalAlignment(g248,g246)
    c: Weight(g249) = 1
    c: Equal(g249,g250)
    c: Equal(g249,g251)
    c: InternalAlignment(g249,g252)
    c: InternalAlignment(g250,g252)
    c: InternalAlignment(g251,g252)
    c: InternalAlignment(g253,g252)
    c: InternalAlignment(g254,g252)
    c: Block(g246)
    c: Block(g252)
    c: Coincident(g255,g246)
    c: Coincident(g255,g252)
    c: Weight(g256) = 1
    c: Equal(g256,g257)
    c: Equal(g256,g258)
    c: InternalAlignment(g256,g259)
    c: InternalAlignment(g257,g259)
    c: InternalAlignment(g258,g259)
    c: InternalAlignment(g260,g259)
    c: InternalAlignment(g261,g259)
    c: Weight(g262) = 1
    c: Equal(g262,g263)
    c: Equal(g262,g264)
    c: InternalAlignment(g262,g265)
    c: InternalAlignment(g263,g265)
    c: InternalAlignment(g264,g265)
    c: InternalAlignment(g266,g265)
    c: InternalAlignment(g267,g265)
    c: Weight(g268) = 1
    c: Equal(g268,g269)
    c: Equal(g268,g270)
    c: InternalAlignment(g268,g271)
    c: InternalAlignment(g269,g271)
    c: InternalAlignment(g270,g271)
    c: InternalAlignment(g272,g271)
    c: InternalAlignment(g273,g271)
    c: Block(g271)
    c: Block(g265)
    c: Block(g259)
    c: Coincident(g274,g265)
    c: Coincident(g274,g259)
    c: Coincident(g275,g259)
    c: Coincident(g275,g271)
    c: Vertical(g275)
    c: Coincident(g276,g271)
    c: Coincident(g276,g265)
    c: Horizontal(g276)
    c: Weight(g277) = 1
    c: Equal(g277,g278)
    c: InternalAlignment(g277,g279)
    c: InternalAlignment(g278,g279)
    c: InternalAlignment(g280,g279)
    c: InternalAlignment(g281,g279)
    c: Weight(g282) = 1
    c: InternalAlignment(g283,g285)
    c: InternalAlignment(g284,g285)
    c: InternalAlignment(g286,g285)
    c: InternalAlignment(g287,g285)
    c: Weight(g288) = 1
    c: Equal(g288,g289)
    c: Equal(g288,g290)
    c: InternalAlignment(g288,g291)
    c: InternalAlignment(g289,g291)
    c: InternalAlignment(g290,g291)
    c: InternalAlignment(g292,g291)
    c: InternalAlignment(g293,g291)
    c: Equal(g294,g295)
    c: Equal(g294,g296)
    c: InternalAlignment(g294,g297)
    c: InternalAlignment(g295,g297)
    c: InternalAlignment(g296,g297)
    c: InternalAlignment(g298,g297)
    c: InternalAlignment(g299,g297)
    c: Block(g285)
    c: Block(g291)
    c: Block(g297)
    c: Block(g279)
    c: Coincident(g300,g279)
    c: Coincident(g300,g285)
    c: Horizontal(g300)
    c: Coincident(g301,g285)
    c: Coincident(g301,g291)
    c: Vertical(g301)
    c: Coincident(g302,g291)
    c: Coincident(g302,g297)
    c: Horizontal(g302)
    c: Coincident(g303,g297)
    c: Coincident(g303,g279)
    c: Weight(g304) = 1
    c: Equal(g304,g305)
    c: Equal(g304,g306)
    c: InternalAlignment(g304,g307)
    c: InternalAlignment(g305,g307)
    c: InternalAlignment(g306,g307)
    c: InternalAlignment(g308,g307)
    c: InternalAlignment(g309,g307)
    c: Weight(g310) = 1
    c: Equal(g310,g311)
    c: Equal(g310,g312)
    c: InternalAlignment(g310,g313)
    c: InternalAlignment(g311,g313)
    c: InternalAlignment(g312,g313)
    c: InternalAlignment(g314,g313)
    c: InternalAlignment(g315,g313)
    c: Weight(g316) = 1
    c: Equal(g316,g317)
    c: Equal(g316,g318)
    c: InternalAlignment(g316,g319)
    c: InternalAlignment(g317,g319)
    c: InternalAlignment(g318,g319)
    c: InternalAlignment(g320,g319)
    c: InternalAlignment(g321,g319)
    c: Block(g319)
    c: Block(g313)
    c: Block(g307)
    c: Coincident(g322,g319)
    c: Coincident(g322,g313)
    c: Horizontal(g322)
    c: Coincident(g323,g313)
    c: Coincident(g323,g307)
    c: Vertical(g323)
    c: Coincident(g324,g307)
    c: Coincident(g324,g319)
    c: InternalAlignment(g325,g326)
    c: InternalAlignment(g327,g326)
    c: InternalAlignment(g328,g326)
    c: Block(g326)
    c: Equal(g329,g330)
    c: Equal(g329,g331)
    c: InternalAlignment(g329,g332)
    c: InternalAlignment(g330,g332)
    c: InternalAlignment(g331,g332)
    c: InternalAlignment(g333,g332)
    c: InternalAlignment(g334,g332)
    c: Block(g332)
    c: Coincident(g335,g326)
    c: Horizontal(g335)
    c: Block(g335)
    c: Coincident(g336,g326)
    c: Coincident(g336,g252)
    c: Vertical(g336)
    c: Coincident(g337,g332)
    c: Coincident(g337,g246)
    c: Vertical(g337)
    c: Block(g338)
    c: Block(g2)
    c: Distance(g336) = 119.89
    c: Coincident(g339,g338)
    c: Coincident(g339,g2)
    c: Coincident(g340,g2)
    c: Coincident(g340,g338)
    c: Block(g3)
    c: Block(g341)
    c: Coincident(g342,g341)
    c: Coincident(g342,g3)
    c: Coincident(g343,g341)
    c: Coincident(g343,g3)
    c: Block(g343)
    c: Block(g342)
    c: Weight(g344) = 1
    c: Equal(g344,g345)
    c: Equal(g344,g346)
    c: InternalAlignment(g344,g347)
    c: InternalAlignment(g345,g347)
    c: InternalAlignment(g346,g347)
    c: InternalAlignment(g348,g347)
    c: InternalAlignment(g349,g347)
    c: Weight(g350) = 1
    c: Equal(g350,g351)
    c: Equal(g350,g352)
    c: InternalAlignment(g350,g353)
    c: InternalAlignment(g351,g353)
    c: InternalAlignment(g352,g353)
    c: InternalAlignment(g354,g353)
    c: InternalAlignment(g355,g353)
    c: Weight(g356) = 1
    c: Equal(g356,g357)
    c: Equal(g356,g358)
    c: InternalAlignment(g356,g359)
    c: InternalAlignment(g357,g359)
    c: InternalAlignment(g358,g359)
    c: InternalAlignment(g360,g359)
    c: InternalAlignment(g361,g359)
    c: Weight(g362) = 1
    c: Equal(g362,g363)
    c: Equal(g362,g364)
    c: InternalAlignment(g362,g365)
    c: InternalAlignment(g363,g365)
    c: InternalAlignment(g364,g365)
    c: InternalAlignment(g366,g365)
    c: InternalAlignment(g367,g365)
    c: Block(g365)
    c: Block(g359)
    c: Block(g353)
    c: Block(g347)
    c: Coincident(g368,g365)
    c: Coincident(g368,g347)
    c: Vertical(g368)
    c: Coincident(g369,g347)
    c: Coincident(g369,g353)
    c: Coincident(g370,g353)
    c: Coincident(g370,g359)
    c: Vertical(g370)
    c: Coincident(g371,g359)
    c: Coincident(g371,g365)
    c: Horizontal(g371)
    c: Vertical(g372)
    c: Block(g372)
    c: Coincident(g373,g372)
    c: Horizontal(g373)
    c: Distance(g373) = 50
    c: Coincident(g374,g372)
    c: Horizontal(g374)
    c: Distance(g374) = 50
    c: Coincident(g375,g373)
    c: Vertical(g375)
    c: Coincident(g376,g374)
    c: Vertical(g376)
    c: Coincident(g377,g374)
    c: Horizontal(g377)
FEATURE [Part::Extrusion] Extrude005
  Base = -> Sketch003
  Dir = (0,0,1)
  DirMode = 2
  FaceMakerClass = Part::FaceMakerBullseye
  LengthFwd = 24
  LengthRev = 0
  Solid = true
  Symmetric = false
